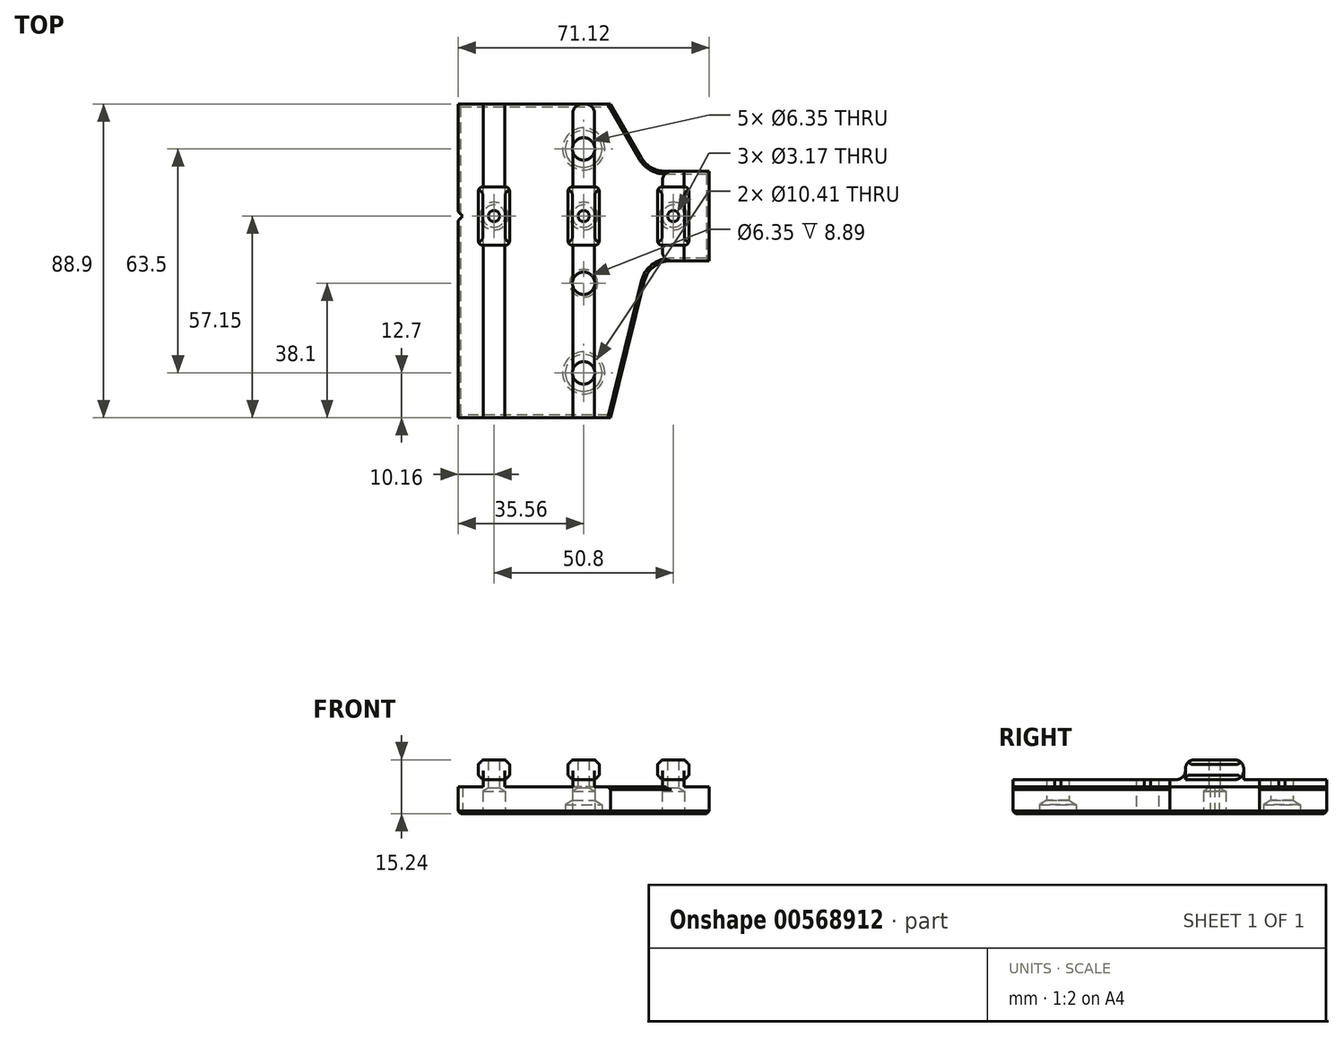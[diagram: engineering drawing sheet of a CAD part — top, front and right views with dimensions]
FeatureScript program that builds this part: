
annotation { "Feature Type Name" : "Feature", "Feature Type Description" : "" }
export const myFeature = defineFeature(function(context is Context, id is Id, definition is map)
    precondition{}
    {
        {
            var Q0;
            Q0=qCreatedBy(makeId("Front.planeOp"),FACE);
            var sketch = newSketch(context, id + "F0", { "sketchPlane" : qUnion([Q0])});
            skLineSegment(sketch, "E0", {"start": v(-35.56, 0) * mm, "end": v(35.56, 0) * mm});
            skLineSegment(sketch, "E1", {"start": v(35.56, 0) * mm, "end": v(35.56, 7.62) * mm});
            skLineSegment(sketch, "E2", {"start": v(35.56, 7.62) * mm, "end": v(28.45, 7.62) * mm});
            skLineSegment(sketch, "E3", {"start": v(28.45, 7.62) * mm, "end": v(28.45, 9.65) * mm});
            skLineSegment(sketch, "E4", {"start": v(28.45, 9.65) * mm, "end": v(22.35, 9.65) * mm});
            skLineSegment(sketch, "E5", {"start": v(22.35, 9.65) * mm, "end": v(22.35, 7.62) * mm});
            skLineSegment(sketch, "E6", {"start": v(22.35, 7.62) * mm, "end": v(3.05, 7.62) * mm});
            skLineSegment(sketch, "E7", {"start": v(3.05, 7.62) * mm, "end": v(3.05, 9.65) * mm});
            skLineSegment(sketch, "E8", {"start": v(3.05, 9.65) * mm, "end": v(-3.05, 9.65) * mm});
            skLineSegment(sketch, "E9", {"start": v(-3.05, 9.65) * mm, "end": v(-3.05, 7.62) * mm});
            skLineSegment(sketch, "E10", {"start": v(-3.05, 7.62) * mm, "end": v(-22.35, 7.62) * mm});
            skLineSegment(sketch, "E11", {"start": v(-22.35, 7.62) * mm, "end": v(-22.35, 9.65) * mm});
            skLineSegment(sketch, "E12", {"start": v(-22.35, 9.65) * mm, "end": v(-28.45, 9.65) * mm});
            skLineSegment(sketch, "E13", {"start": v(-28.45, 9.65) * mm, "end": v(-28.45, 7.62) * mm});
            skLineSegment(sketch, "E14", {"start": v(-28.45, 7.62) * mm, "end": v(-35.56, 7.62) * mm});
            skLineSegment(sketch, "E15", {"start": v(-35.56, 7.62) * mm, "end": v(-35.56, 0) * mm});
            skSolve(sketch);
        }
        {
            var Q0;
            Q0 = qSketchRegion(id + "F0", true);
            extrude(context, id + "F1", {"entities" : qUnion([Q0]), "endBound" : BoundingType.SYMMETRIC, "depth" : 88.9 * mm, "offsetDistance" : 25.4 * mm});
        }
        {
            var Q0;
            Q0=makeQuery(id+"F1.opExtrude","SWEPT_FACE",FACE,{"disambiguationData":[OSD([sQuery(id+"F0.wireOp",EDGE,"E0")])]});
            var sketch = newSketch(context, id + "F2", { "sketchPlane" : qUnion([Q0])});
            skPoint(sketch, "E16", {"position": v(0, -31.75) * mm});
            skPoint(sketch, "E17", {"position": v(25.4, -12.7) * mm});
            skPoint(sketch, "E18", {"position": v(0, -12.7) * mm});
            skPoint(sketch, "E19", {"position": v(-25.4, -12.7) * mm});
            skPoint(sketch, "E20", {"position": v(0, 6.35) * mm});
            skPoint(sketch, "E21", {"position": v(0, 31.75) * mm});
            skSolve(sketch);
        }
        {
            var Q0;
            {var subQ0=sQuery(id+"F0.wireOp",EDGE,"E0");Q0=makeQuery(id+"F2.imprint","IMPRINT",FACE,{"disambiguationData":[TD([[makeQuery(id+"F2.imprint","IMPRINT",EDGE,{"derivedFrom":makeQuery(id+"F1.opExtrude","CAP_EDGE",EDGE,{"disambiguationData":[OSD([subQ0])],"isStart":true})}),1.0]])]});}
            var sketch = newSketch(context, id + "F3", { "sketchPlane" : qUnion([Q0])});
            skLineSegment(sketch, "E22", {"start": v(35.56, -44.45) * mm, "end": v(7.62, -44.45) * mm});
            skLineSegment(sketch, "E23", {"start": v(7.62, -44.45) * mm, "end": v(18.62, -25.4) * mm});
            skLineSegment(sketch, "E24", {"start": v(18.62, -25.4) * mm, "end": v(35.56, -25.4) * mm});
            skLineSegment(sketch, "E25", {"start": v(35.56, -25.4) * mm, "end": v(35.56, -44.45) * mm});
            skLineSegment(sketch, "E26", {"start": v(35.56, 44.45) * mm, "end": v(35.56, 0) * mm});
            skLineSegment(sketch, "E27", {"start": v(35.56, 0) * mm, "end": v(18.62, 0) * mm});
            skLineSegment(sketch, "E28", {"start": v(18.62, 0) * mm, "end": v(7.62, 44.45) * mm});
            skLineSegment(sketch, "E29", {"start": v(7.62, 44.45) * mm, "end": v(35.56, 44.45) * mm});
            skSolve(sketch);
        }
        {
            var Q0;
            Q0=makeQuery(id+"F3.imprint","IMPRINT",FACE,{"disambiguationData":[TD([[makeQuery(id+"F3.imprint","IMPRINT",EDGE,{"derivedFrom":sQuery(id+"F3.wireOp",EDGE,"E22")}),1.0]])]});
            var Q1;
            Q1=makeQuery(id+"F3.imprint","IMPRINT",FACE,{"disambiguationData":[TD([[makeQuery(id+"F3.imprint","IMPRINT",EDGE,{"derivedFrom":sQuery(id+"F3.wireOp",EDGE,"E26")}),-1.0]])]});
            extrude(context, id + "F4", {"entities" : qUnion([Q0, Q1]), "operationType" : NewBodyOperationType.REMOVE, "oppositeDirection" : true, "depth" : 25.4 * mm, "offsetDistance" : 25.4 * mm});
        }
        {
            var Q0;
            Q0=sQuery(id+"F2.wireOp",VERTEX,"E16");
            var Q1;
            Q1=sQuery(id+"F2.wireOp",VERTEX,"E20");
            var Q2;
            Q2=sQuery(id+"F2.wireOp",VERTEX,"E21");
            var Q3;
            Q3=makeQuery(id+"F1.opExtrude","SWEPT_BODY",BODY,{"disambiguationData":[OSD([sQuery(id+"F0.wireOp",EDGE,"E0"),sQuery(id+"F0.wireOp",EDGE,"E1"),sQuery(id+"F0.wireOp",EDGE,"E2"),sQuery(id+"F0.wireOp",EDGE,"E3"),sQuery(id+"F0.wireOp",EDGE,"E4"),sQuery(id+"F0.wireOp",EDGE,"E5"),sQuery(id+"F0.wireOp",EDGE,"E6"),sQuery(id+"F0.wireOp",EDGE,"E7"),sQuery(id+"F0.wireOp",EDGE,"E8"),sQuery(id+"F0.wireOp",EDGE,"E9"),sQuery(id+"F0.wireOp",EDGE,"E10"),sQuery(id+"F0.wireOp",EDGE,"E11"),sQuery(id+"F0.wireOp",EDGE,"E12"),sQuery(id+"F0.wireOp",EDGE,"E13"),sQuery(id+"F0.wireOp",EDGE,"E14"),sQuery(id+"F0.wireOp",EDGE,"E15")])]});
            hole(context, id + "F5", {"style" : HoleStyle.SIMPLE, "endStyle" : HoleEndStyle.THROUGH, "holeDiameter" : 6.35 * mm, "tappedDepth" : 12.7 * mm, "tapClearance" : 3, "startFromSketch" : true, "locations" : qUnion([Q0, Q1, Q2]), "scope" : qUnion([Q3])});
        }
        {
            var Q0;
            Q0=sQuery(id+"F2.wireOp",VERTEX,"E19");
            var Q1;
            Q1=sQuery(id+"F2.wireOp",VERTEX,"E18");
            var Q2;
            Q2=sQuery(id+"F2.wireOp",VERTEX,"E17");
            var Q3;
            Q3=makeQuery(id+"F1.opExtrude","SWEPT_BODY",BODY,{"disambiguationData":[OSD([sQuery(id+"F0.wireOp",EDGE,"E0"),sQuery(id+"F0.wireOp",EDGE,"E1"),sQuery(id+"F0.wireOp",EDGE,"E2"),sQuery(id+"F0.wireOp",EDGE,"E3"),sQuery(id+"F0.wireOp",EDGE,"E4"),sQuery(id+"F0.wireOp",EDGE,"E5"),sQuery(id+"F0.wireOp",EDGE,"E6"),sQuery(id+"F0.wireOp",EDGE,"E7"),sQuery(id+"F0.wireOp",EDGE,"E8"),sQuery(id+"F0.wireOp",EDGE,"E9"),sQuery(id+"F0.wireOp",EDGE,"E10"),sQuery(id+"F0.wireOp",EDGE,"E11"),sQuery(id+"F0.wireOp",EDGE,"E12"),sQuery(id+"F0.wireOp",EDGE,"E13"),sQuery(id+"F0.wireOp",EDGE,"E14"),sQuery(id+"F0.wireOp",EDGE,"E15")])]});
            hole(context, id + "F6", {"style" : HoleStyle.SIMPLE, "endStyle" : HoleEndStyle.BLIND, "holeDiameter" : 6.35 * mm, "holeDepth" : 6.35 * mm, "tappedDepth" : 12.7 * mm, "tapClearance" : 3, "startFromSketch" : true, "locations" : qUnion([Q0, Q1, Q2]), "scope" : qUnion([Q3])});
        }
        {
            var Q0;
            {var subQ0=sQuery(id+"F0.wireOp",EDGE,"E7");var subQ2=sQuery(id+"F0.wireOp",EDGE,"E9");var subQ4=makeQuery(id+"F5.hole-0.opRevolve","SWEPT_FACE",FACE,{"disambiguationData":[OSD([sQuery(id+"F5.hole-0.sketch.wireOp",EDGE,"core_line_2")])]});var subQ5=sQuery(id+"F0.wireOp",EDGE,"E8");Q0=makeQuery(id+"F5.hole-1.boolean.opBoolean","SPLIT",FACE,{"disambiguationData":[TD([makeQuery(id+"F5.hole-0.boolean.opBoolean","COPY",FACE,{"derivedFrom":subQ4})])],"derivedFrom":makeQuery(id+"F5.hole-0.boolean.opBoolean","SPLIT",FACE,{"disambiguationData":[TD([makeQuery(id+"F1.opExtrude","CAP_FACE",FACE,{"disambiguationData":[OSD([sQuery(id+"F0.wireOp",EDGE,"E0"),sQuery(id+"F0.wireOp",EDGE,"E1"),sQuery(id+"F0.wireOp",EDGE,"E2"),sQuery(id+"F0.wireOp",EDGE,"E3"),sQuery(id+"F0.wireOp",EDGE,"E4"),sQuery(id+"F0.wireOp",EDGE,"E5"),sQuery(id+"F0.wireOp",EDGE,"E6"),subQ0,subQ5,subQ2,sQuery(id+"F0.wireOp",EDGE,"E10"),sQuery(id+"F0.wireOp",EDGE,"E11"),sQuery(id+"F0.wireOp",EDGE,"E12"),sQuery(id+"F0.wireOp",EDGE,"E13"),sQuery(id+"F0.wireOp",EDGE,"E14"),sQuery(id+"F0.wireOp",EDGE,"E15")])],"isStart":false})])],"derivedFrom":makeQuery(id+"F1.opExtrude","SWEPT_FACE",FACE,{"disambiguationData":[OSD([subQ5])]})})});}
            var sketch = newSketch(context, id + "F7", { "sketchPlane" : qUnion([Q0])});
            skLineSegment(sketch, "E30.bottom", {"start": v(-29.85, 20.96) * mm, "end": v(-20.96, 20.96) * mm});
            skLineSegment(sketch, "E30.top", {"start": v(-29.85, 4.44) * mm, "end": v(-20.96, 4.44) * mm});
            skLineSegment(sketch, "E30.left", {"start": v(-29.84, 20.96) * mm, "end": v(-29.84, 4.44) * mm});
            skLineSegment(sketch, "E30.right", {"start": v(-20.95, 20.96) * mm, "end": v(-20.95, 4.44) * mm});
            skLineSegment(sketch, "E31.bottom", {"start": v(-4.44, 20.96) * mm, "end": v(4.45, 20.96) * mm});
            skLineSegment(sketch, "E31.top", {"start": v(-4.44, 4.44) * mm, "end": v(4.45, 4.44) * mm});
            skLineSegment(sketch, "E31.left", {"start": v(-4.44, 20.95) * mm, "end": v(-4.45, 4.45) * mm});
            skLineSegment(sketch, "E31.right", {"start": v(4.45, 20.95) * mm, "end": v(4.45, 4.45) * mm});
            skLineSegment(sketch, "E32.bottom", {"start": v(20.96, 20.96) * mm, "end": v(29.85, 20.96) * mm});
            skLineSegment(sketch, "E32.top", {"start": v(20.96, 4.44) * mm, "end": v(29.85, 4.44) * mm});
            skLineSegment(sketch, "E32.left", {"start": v(20.96, 20.96) * mm, "end": v(20.95, 4.44) * mm});
            skLineSegment(sketch, "E32.right", {"start": v(29.84, 20.96) * mm, "end": v(29.84, 4.44) * mm});
            skLineSegment(sketch, "E33", {"start": v(-25.4, 20.96) * mm, "end": v(-25.4, 4.44) * mm, "construction": true});
            skLineSegment(sketch, "E34", {"start": v(0, 20.96) * mm, "end": v(0, 4.44) * mm, "construction": true});
            skLineSegment(sketch, "E35", {"start": v(25.4, 20.96) * mm, "end": v(25.4, 4.44) * mm, "construction": true});
            skSolve(sketch);
        }
        {
            var Q0;
            Q0 = qSketchRegion(id + "F7", true);
            extrude(context, id + "F8", {"entities" : qUnion([Q0]), "operationType" : NewBodyOperationType.ADD, "depth" : 5.6 * mm, "offsetDistance" : 25.4 * mm});
        }
        {
            var Q0;
            Q0=makeQuery(id+"F8.opExtrude","CAP_EDGE",EDGE,{"disambiguationData":[OSD([sQuery(id+"F7.wireOp",EDGE,"E30.left")])],"isStart":true});
            var Q1;
            Q1=makeQuery(id+"F8.opExtrude","CAP_EDGE",EDGE,{"disambiguationData":[OSD([sQuery(id+"F7.wireOp",EDGE,"E30.left")])],"isStart":false});
            var Q2;
            Q2=makeQuery(id+"F8.opExtrude","CAP_EDGE",EDGE,{"disambiguationData":[OSD([sQuery(id+"F7.wireOp",EDGE,"E30.right")])],"isStart":false});
            var Q3;
            Q3=makeQuery(id+"F8.opExtrude","CAP_EDGE",EDGE,{"disambiguationData":[OSD([sQuery(id+"F7.wireOp",EDGE,"E31.left")])],"isStart":true});
            var Q4;
            Q4=makeQuery(id+"F8.opExtrude","CAP_EDGE",EDGE,{"disambiguationData":[OSD([sQuery(id+"F7.wireOp",EDGE,"E31.left")])],"isStart":false});
            var Q5;
            Q5=makeQuery(id+"F8.opExtrude","CAP_EDGE",EDGE,{"disambiguationData":[OSD([sQuery(id+"F7.wireOp",EDGE,"E32.left")])],"isStart":true});
            var Q6;
            Q6=makeQuery(id+"F8.opExtrude","CAP_EDGE",EDGE,{"disambiguationData":[OSD([sQuery(id+"F7.wireOp",EDGE,"E32.left")])],"isStart":false});
            var Q7;
            Q7=makeQuery(id+"F8.opExtrude","CAP_EDGE",EDGE,{"disambiguationData":[OSD([sQuery(id+"F7.wireOp",EDGE,"E31.right")])],"isStart":false});
            var Q8;
            Q8=makeQuery(id+"F8.opExtrude","CAP_EDGE",EDGE,{"disambiguationData":[OSD([sQuery(id+"F7.wireOp",EDGE,"E30.right")])],"isStart":true});
            var Q9;
            Q9=makeQuery(id+"F8.opExtrude","CAP_EDGE",EDGE,{"disambiguationData":[OSD([sQuery(id+"F7.wireOp",EDGE,"E31.right")])],"isStart":true});
            var Q10;
            Q10=makeQuery(id+"F8.opExtrude","CAP_EDGE",EDGE,{"disambiguationData":[OSD([sQuery(id+"F7.wireOp",EDGE,"E32.right")])],"isStart":true});
            var Q11;
            Q11=makeQuery(id+"F8.opExtrude","CAP_EDGE",EDGE,{"disambiguationData":[OSD([sQuery(id+"F7.wireOp",EDGE,"E32.right")])],"isStart":false});
            chamfer(context, id + "F9", {"entities" : qUnion([Q0, Q1, Q2, Q3, Q4, Q5, Q6, Q7, Q8, Q9, Q10, Q11]), "width" : 1.27 * mm, "tangentPropagation" : true});
        }
        {
            var Q0;
            Q0=sQuery(id+"F2.wireOp",VERTEX,"E19");
            var Q1;
            Q1=sQuery(id+"F2.wireOp",VERTEX,"E18");
            var Q2;
            Q2=sQuery(id+"F2.wireOp",VERTEX,"E17");
            var Q3;
            Q3=makeQuery(id+"F1.opExtrude","SWEPT_BODY",BODY,{"disambiguationData":[OSD([sQuery(id+"F0.wireOp",EDGE,"E0"),sQuery(id+"F0.wireOp",EDGE,"E1"),sQuery(id+"F0.wireOp",EDGE,"E2"),sQuery(id+"F0.wireOp",EDGE,"E3"),sQuery(id+"F0.wireOp",EDGE,"E4"),sQuery(id+"F0.wireOp",EDGE,"E5"),sQuery(id+"F0.wireOp",EDGE,"E6"),sQuery(id+"F0.wireOp",EDGE,"E7"),sQuery(id+"F0.wireOp",EDGE,"E8"),sQuery(id+"F0.wireOp",EDGE,"E9"),sQuery(id+"F0.wireOp",EDGE,"E10"),sQuery(id+"F0.wireOp",EDGE,"E11"),sQuery(id+"F0.wireOp",EDGE,"E12"),sQuery(id+"F0.wireOp",EDGE,"E13"),sQuery(id+"F0.wireOp",EDGE,"E14"),sQuery(id+"F0.wireOp",EDGE,"E15")])]});
            hole(context, id + "F10", {"style" : HoleStyle.SIMPLE, "endStyle" : HoleEndStyle.THROUGH, "holeDiameter" : 3.17 * mm, "tappedDepth" : 12.7 * mm, "tapClearance" : 3, "startFromSketch" : true, "locations" : qUnion([Q0, Q1, Q2]), "scope" : qUnion([Q3])});
        }
        {
            var Q0;
            Q0=sQuery(id+"F2.wireOp",VERTEX,"E16");
            var Q1;
            Q1=sQuery(id+"F2.wireOp",VERTEX,"E21");
            var Q2;
            Q2=makeQuery(id+"F1.opExtrude","SWEPT_BODY",BODY,{"disambiguationData":[OSD([sQuery(id+"F0.wireOp",EDGE,"E0"),sQuery(id+"F0.wireOp",EDGE,"E1"),sQuery(id+"F0.wireOp",EDGE,"E2"),sQuery(id+"F0.wireOp",EDGE,"E3"),sQuery(id+"F0.wireOp",EDGE,"E4"),sQuery(id+"F0.wireOp",EDGE,"E5"),sQuery(id+"F0.wireOp",EDGE,"E6"),sQuery(id+"F0.wireOp",EDGE,"E7"),sQuery(id+"F0.wireOp",EDGE,"E8"),sQuery(id+"F0.wireOp",EDGE,"E9"),sQuery(id+"F0.wireOp",EDGE,"E10"),sQuery(id+"F0.wireOp",EDGE,"E11"),sQuery(id+"F0.wireOp",EDGE,"E12"),sQuery(id+"F0.wireOp",EDGE,"E13"),sQuery(id+"F0.wireOp",EDGE,"E14"),sQuery(id+"F0.wireOp",EDGE,"E15")])]});
            hole(context, id + "F11", {"style" : HoleStyle.SIMPLE, "endStyle" : HoleEndStyle.BLIND, "holeDiameter" : 10.4 * mm, "holeDepth" : 2.54 * mm, "tappedDepth" : 12.7 * mm, "tapClearance" : 3, "startFromSketch" : true, "locations" : qUnion([Q0, Q1]), "scope" : qUnion([Q2])});
        }
        {
            var Q0;
            Q0=makeQuery(id+"F6yBhReDyAXkrBv_1.1.F4.boolean.opBoolean","COPY",EDGE,{"derivedFrom":makeQuery(id+"F6yBhReDyAXkrBv_1.1.F4.opExtrude","SWEPT_EDGE",EDGE,{"disambiguationData":[OSD([sQuery(id+"F3.wireOp",EDGE,"E27"),sQuery(id+"F3.wireOp",EDGE,"E28")])]})});
            var Q1;
            Q1=makeQuery(id+"F4.boolean.opBoolean","COPY",EDGE,{"derivedFrom":makeQuery(id+"F4.opExtrude","SWEPT_EDGE",EDGE,{"disambiguationData":[OSD([sQuery(id+"F3.wireOp",EDGE,"E27"),sQuery(id+"F3.wireOp",EDGE,"E28")])]})});
            var Q2;
            Q2=makeQuery(id+"F4.boolean.opBoolean","COPY",EDGE,{"derivedFrom":makeQuery(id+"F4.opExtrude","SWEPT_EDGE",EDGE,{"disambiguationData":[OSD([sQuery(id+"F3.wireOp",EDGE,"E23"),sQuery(id+"F3.wireOp",EDGE,"E24")])]})});
            var Q3;
            Q3=makeQuery(id+"F6yBhReDyAXkrBv_1.1.F4.boolean.opBoolean","COPY",EDGE,{"derivedFrom":makeQuery(id+"F6yBhReDyAXkrBv_1.1.F4.opExtrude","SWEPT_EDGE",EDGE,{"disambiguationData":[OSD([sQuery(id+"F3.wireOp",EDGE,"E23"),sQuery(id+"F3.wireOp",EDGE,"E24")])]})});
            var Q4;
            Q4=makeQuery(id+"F6yBhReDyAXkrBv_1.1.F4.boolean.opBoolean","COPY",EDGE,{"derivedFrom":makeQuery(id+"F6yBhReDyAXkrBv_1.1.F4.opExtrude","SWEPT_EDGE",EDGE,{"disambiguationData":[OSD([sQuery(id+"F0.wireOp",EDGE,"E0"),sQuery(id+"F0.wireOp",EDGE,"E1"),sQuery(id+"F3.wireOp",EDGE,"E24"),sQuery(id+"F3.wireOp",EDGE,"E25")])]})});
            var Q5;
            Q5=makeQuery(id+"F6yBhReDyAXkrBv_1.1.F4.boolean.opBoolean","COPY",EDGE,{"derivedFrom":makeQuery(id+"F6yBhReDyAXkrBv_1.1.F4.opExtrude","SWEPT_EDGE",EDGE,{"disambiguationData":[OSD([sQuery(id+"F0.wireOp",EDGE,"E0"),sQuery(id+"F0.wireOp",EDGE,"E1"),sQuery(id+"F3.wireOp",EDGE,"E26"),sQuery(id+"F3.wireOp",EDGE,"E27")])]})});
            var Q6;
            Q6=makeQuery(id+"F6yBhReDyAXkrBv_1.1.F4.boolean.opBoolean","COPY",EDGE,{"derivedFrom":makeQuery(id+"F6yBhReDyAXkrBv_1.1.F4.opExtrude","SWEPT_EDGE",EDGE,{"disambiguationData":[OSD([sQuery(id+"F0.wireOp",EDGE,"E0"),sQuery(id+"F3.wireOp",EDGE,"E28"),sQuery(id+"F3.wireOp",EDGE,"E29")])]})});
            var Q7;
            Q7=makeQuery(id+"F6yBhReDyAXkrBv_1.1.F4.boolean.opBoolean","COPY",EDGE,{"derivedFrom":makeQuery(id+"F6yBhReDyAXkrBv_1.1.F4.opExtrude","SWEPT_EDGE",EDGE,{"disambiguationData":[OSD([sQuery(id+"F0.wireOp",EDGE,"E0"),sQuery(id+"F3.wireOp",EDGE,"E22"),sQuery(id+"F3.wireOp",EDGE,"E23")])]})});
            var Q8;
            Q8=makeQuery(id+"F4.boolean.opBoolean","COPY",EDGE,{"derivedFrom":makeQuery(id+"F4.opExtrude","SWEPT_EDGE",EDGE,{"disambiguationData":[OSD([sQuery(id+"F0.wireOp",EDGE,"E0"),sQuery(id+"F3.wireOp",EDGE,"E22"),sQuery(id+"F3.wireOp",EDGE,"E23")])]})});
            var Q9;
            Q9=makeQuery(id+"F4.boolean.opBoolean","COPY",EDGE,{"derivedFrom":makeQuery(id+"F4.opExtrude","SWEPT_EDGE",EDGE,{"disambiguationData":[OSD([sQuery(id+"F0.wireOp",EDGE,"E0"),sQuery(id+"F0.wireOp",EDGE,"E1"),sQuery(id+"F3.wireOp",EDGE,"E24"),sQuery(id+"F3.wireOp",EDGE,"E25")])]})});
            var Q10;
            Q10=makeQuery(id+"F4.boolean.opBoolean","COPY",EDGE,{"derivedFrom":makeQuery(id+"F4.opExtrude","SWEPT_EDGE",EDGE,{"disambiguationData":[OSD([sQuery(id+"F0.wireOp",EDGE,"E0"),sQuery(id+"F0.wireOp",EDGE,"E1"),sQuery(id+"F3.wireOp",EDGE,"E26"),sQuery(id+"F3.wireOp",EDGE,"E27")])]})});
            var Q11;
            Q11=makeQuery(id+"F4.boolean.opBoolean","COPY",EDGE,{"derivedFrom":makeQuery(id+"F4.opExtrude","SWEPT_EDGE",EDGE,{"disambiguationData":[OSD([sQuery(id+"F0.wireOp",EDGE,"E0"),sQuery(id+"F3.wireOp",EDGE,"E28"),sQuery(id+"F3.wireOp",EDGE,"E29")])]})});
            fillet(context, id + "F12", {"entities" : qUnion([Q0, Q1, Q2, Q3, Q4, Q5, Q6, Q7, Q8, Q9, Q10, Q11]), "radius" : 7.62 * mm, "tangentPropagation" : true, "allowEdgeOverflow" : false});
        }
        {
            var Q0;
            Q0=makeQuery(id+"F12.opFillet","BLEND_EDGE",EDGE,{"blendedFrom":[makeQuery(id+"F6yBhReDyAXkrBv_1.1.F4.boolean.opBoolean","COPY",EDGE,{"derivedFrom":makeQuery(id+"F6yBhReDyAXkrBv_1.1.F4.opExtrude","SWEPT_EDGE",EDGE,{"disambiguationData":[OSD([sQuery(id+"F0.wireOp",EDGE,"E0"),sQuery(id+"F0.wireOp",EDGE,"E1"),sQuery(id+"F3.wireOp",EDGE,"E26"),sQuery(id+"F3.wireOp",EDGE,"E27")])]})}),makeQuery(id+"F1.opExtrude","SWEPT_FACE",FACE,{"disambiguationData":[OSD([sQuery(id+"F0.wireOp",EDGE,"E13")])]})],"blendedInto":[makeQuery(id+"F1.opExtrude","SWEPT_FACE",FACE,{"disambiguationData":[OSD([sQuery(id+"F0.wireOp",EDGE,"E13")])]})]});
            var Q1;
            Q1=makeQuery(id+"F12.opFillet","BLEND_EDGE",EDGE,{"blendedFrom":[makeQuery(id+"F6yBhReDyAXkrBv_1.1.F4.boolean.opBoolean","COPY",EDGE,{"derivedFrom":makeQuery(id+"F6yBhReDyAXkrBv_1.1.F4.opExtrude","SWEPT_EDGE",EDGE,{"disambiguationData":[OSD([sQuery(id+"F3.wireOp",EDGE,"E27"),sQuery(id+"F3.wireOp",EDGE,"E28")])]})}),makeQuery(id+"F1.opExtrude","SWEPT_FACE",FACE,{"disambiguationData":[OSD([sQuery(id+"F0.wireOp",EDGE,"E11")])]})],"blendedInto":[makeQuery(id+"F1.opExtrude","SWEPT_FACE",FACE,{"disambiguationData":[OSD([sQuery(id+"F0.wireOp",EDGE,"E11")])]})]});
            var Q2;
            {var subQ0=sQuery(id+"F0.wireOp",EDGE,"E10");var subQ1=sQuery(id+"F0.wireOp",EDGE,"E9");var subQ2=sQuery(id+"F0.wireOp",EDGE,"E8");var subQ3=sQuery(id+"F0.wireOp",EDGE,"E0");var subQ4=makeQuery(id+"F1.opExtrude","CAP_FACE",FACE,{"disambiguationData":[OSD([subQ3,sQuery(id+"F0.wireOp",EDGE,"E1"),sQuery(id+"F0.wireOp",EDGE,"E2"),sQuery(id+"F0.wireOp",EDGE,"E3"),sQuery(id+"F0.wireOp",EDGE,"E4"),sQuery(id+"F0.wireOp",EDGE,"E5"),sQuery(id+"F0.wireOp",EDGE,"E6"),sQuery(id+"F0.wireOp",EDGE,"E7"),subQ2,subQ1,subQ0,sQuery(id+"F0.wireOp",EDGE,"E11"),sQuery(id+"F0.wireOp",EDGE,"E12"),sQuery(id+"F0.wireOp",EDGE,"E13"),sQuery(id+"F0.wireOp",EDGE,"E14"),sQuery(id+"F0.wireOp",EDGE,"E15")])],"isStart":false});Q2=makeQuery(id+"F12.opFillet","BLEND_EDGE",EDGE,{"blendedFrom":[makeQuery(id+"F6yBhReDyAXkrBv_1.1.F4.boolean.opBoolean","COPY",EDGE,{"derivedFrom":makeQuery(id+"F6yBhReDyAXkrBv_1.1.F4.opExtrude","SWEPT_EDGE",EDGE,{"disambiguationData":[OSD([subQ3,sQuery(id+"F3.wireOp",EDGE,"E28"),sQuery(id+"F3.wireOp",EDGE,"E29")])]})}),makeQuery(id+"F5.hole-2.boolean.opBoolean","SPLIT",FACE,{"disambiguationData":[TD([subQ4])],"derivedFrom":makeQuery(id+"F5.hole-1.boolean.opBoolean","SPLIT",FACE,{"disambiguationData":[TD([subQ4])],"derivedFrom":makeQuery(id+"F5.hole-0.boolean.opBoolean","SPLIT",FACE,{"disambiguationData":[TD([subQ4])],"derivedFrom":makeQuery(id+"F1.opExtrude","SWEPT_FACE",FACE,{"disambiguationData":[OSD([subQ1])]})})})})],"blendedInto":[makeQuery(id+"F5.hole-2.boolean.opBoolean","SPLIT",FACE,{"disambiguationData":[TD([subQ4])],"derivedFrom":makeQuery(id+"F5.hole-1.boolean.opBoolean","SPLIT",FACE,{"disambiguationData":[TD([subQ4])],"derivedFrom":makeQuery(id+"F5.hole-0.boolean.opBoolean","SPLIT",FACE,{"disambiguationData":[TD([subQ4])],"derivedFrom":makeQuery(id+"F1.opExtrude","SWEPT_FACE",FACE,{"disambiguationData":[OSD([subQ1])]})})})})]});}
            var Q3;
            {var subQ0=sQuery(id+"F0.wireOp",EDGE,"E8");var subQ1=sQuery(id+"F0.wireOp",EDGE,"E7");var subQ2=sQuery(id+"F0.wireOp",EDGE,"E6");var subQ3=sQuery(id+"F0.wireOp",EDGE,"E0");var subQ4=makeQuery(id+"F1.opExtrude","CAP_FACE",FACE,{"disambiguationData":[OSD([subQ3,sQuery(id+"F0.wireOp",EDGE,"E1"),sQuery(id+"F0.wireOp",EDGE,"E2"),sQuery(id+"F0.wireOp",EDGE,"E3"),sQuery(id+"F0.wireOp",EDGE,"E4"),sQuery(id+"F0.wireOp",EDGE,"E5"),subQ2,subQ1,subQ0,sQuery(id+"F0.wireOp",EDGE,"E9"),sQuery(id+"F0.wireOp",EDGE,"E10"),sQuery(id+"F0.wireOp",EDGE,"E11"),sQuery(id+"F0.wireOp",EDGE,"E12"),sQuery(id+"F0.wireOp",EDGE,"E13"),sQuery(id+"F0.wireOp",EDGE,"E14"),sQuery(id+"F0.wireOp",EDGE,"E15")])],"isStart":false});Q3=makeQuery(id+"F12.opFillet","BLEND_EDGE",EDGE,{"blendedFrom":[makeQuery(id+"F4.boolean.opBoolean","COPY",EDGE,{"derivedFrom":makeQuery(id+"F4.opExtrude","SWEPT_EDGE",EDGE,{"disambiguationData":[OSD([subQ3,sQuery(id+"F3.wireOp",EDGE,"E28"),sQuery(id+"F3.wireOp",EDGE,"E29")])]})}),makeQuery(id+"F5.hole-2.boolean.opBoolean","SPLIT",FACE,{"disambiguationData":[TD([subQ4])],"derivedFrom":makeQuery(id+"F5.hole-1.boolean.opBoolean","SPLIT",FACE,{"disambiguationData":[TD([subQ4])],"derivedFrom":makeQuery(id+"F5.hole-0.boolean.opBoolean","SPLIT",FACE,{"disambiguationData":[TD([subQ4])],"derivedFrom":makeQuery(id+"F1.opExtrude","SWEPT_FACE",FACE,{"disambiguationData":[OSD([subQ1])]})})})})],"blendedInto":[makeQuery(id+"F5.hole-2.boolean.opBoolean","SPLIT",FACE,{"disambiguationData":[TD([subQ4])],"derivedFrom":makeQuery(id+"F5.hole-1.boolean.opBoolean","SPLIT",FACE,{"disambiguationData":[TD([subQ4])],"derivedFrom":makeQuery(id+"F5.hole-0.boolean.opBoolean","SPLIT",FACE,{"disambiguationData":[TD([subQ4])],"derivedFrom":makeQuery(id+"F1.opExtrude","SWEPT_FACE",FACE,{"disambiguationData":[OSD([subQ1])]})})})})]});}
            var Q4;
            Q4=makeQuery(id+"F12.opFillet","BLEND_EDGE",EDGE,{"blendedFrom":[makeQuery(id+"F4.boolean.opBoolean","COPY",EDGE,{"derivedFrom":makeQuery(id+"F4.opExtrude","SWEPT_EDGE",EDGE,{"disambiguationData":[OSD([sQuery(id+"F3.wireOp",EDGE,"E27"),sQuery(id+"F3.wireOp",EDGE,"E28")])]})}),makeQuery(id+"F1.opExtrude","SWEPT_FACE",FACE,{"disambiguationData":[OSD([sQuery(id+"F0.wireOp",EDGE,"E5")])]})],"blendedInto":[makeQuery(id+"F1.opExtrude","SWEPT_FACE",FACE,{"disambiguationData":[OSD([sQuery(id+"F0.wireOp",EDGE,"E5")])]})]});
            var Q5;
            Q5=makeQuery(id+"F12.opFillet","BLEND_EDGE",EDGE,{"blendedFrom":[makeQuery(id+"F4.boolean.opBoolean","COPY",EDGE,{"derivedFrom":makeQuery(id+"F4.opExtrude","SWEPT_EDGE",EDGE,{"disambiguationData":[OSD([sQuery(id+"F0.wireOp",EDGE,"E0"),sQuery(id+"F0.wireOp",EDGE,"E1"),sQuery(id+"F3.wireOp",EDGE,"E26"),sQuery(id+"F3.wireOp",EDGE,"E27")])]})}),makeQuery(id+"F1.opExtrude","SWEPT_FACE",FACE,{"disambiguationData":[OSD([sQuery(id+"F0.wireOp",EDGE,"E3")])]})],"blendedInto":[makeQuery(id+"F1.opExtrude","SWEPT_FACE",FACE,{"disambiguationData":[OSD([sQuery(id+"F0.wireOp",EDGE,"E3")])]})]});
            var Q6;
            Q6=makeQuery(id+"F12.opFillet","BLEND_EDGE",EDGE,{"blendedFrom":[makeQuery(id+"F4.boolean.opBoolean","COPY",EDGE,{"derivedFrom":makeQuery(id+"F4.opExtrude","SWEPT_EDGE",EDGE,{"disambiguationData":[OSD([sQuery(id+"F0.wireOp",EDGE,"E0"),sQuery(id+"F0.wireOp",EDGE,"E1"),sQuery(id+"F3.wireOp",EDGE,"E24"),sQuery(id+"F3.wireOp",EDGE,"E25")])]})}),makeQuery(id+"F1.opExtrude","SWEPT_FACE",FACE,{"disambiguationData":[OSD([sQuery(id+"F0.wireOp",EDGE,"E3")])]})],"blendedInto":[makeQuery(id+"F1.opExtrude","SWEPT_FACE",FACE,{"disambiguationData":[OSD([sQuery(id+"F0.wireOp",EDGE,"E3")])]})]});
            var Q7;
            Q7=makeQuery(id+"F12.opFillet","BLEND_EDGE",EDGE,{"blendedFrom":[makeQuery(id+"F4.boolean.opBoolean","COPY",EDGE,{"derivedFrom":makeQuery(id+"F4.opExtrude","SWEPT_EDGE",EDGE,{"disambiguationData":[OSD([sQuery(id+"F3.wireOp",EDGE,"E23"),sQuery(id+"F3.wireOp",EDGE,"E24")])]})}),makeQuery(id+"F1.opExtrude","SWEPT_FACE",FACE,{"disambiguationData":[OSD([sQuery(id+"F0.wireOp",EDGE,"E5")])]})],"blendedInto":[makeQuery(id+"F1.opExtrude","SWEPT_FACE",FACE,{"disambiguationData":[OSD([sQuery(id+"F0.wireOp",EDGE,"E5")])]})]});
            var Q8;
            Q8=makeQuery(id+"F12.opFillet","BLEND_EDGE",EDGE,{"blendedFrom":[makeQuery(id+"F6yBhReDyAXkrBv_1.1.F4.boolean.opBoolean","COPY",EDGE,{"derivedFrom":makeQuery(id+"F6yBhReDyAXkrBv_1.1.F4.opExtrude","SWEPT_EDGE",EDGE,{"disambiguationData":[OSD([sQuery(id+"F0.wireOp",EDGE,"E0"),sQuery(id+"F0.wireOp",EDGE,"E1"),sQuery(id+"F3.wireOp",EDGE,"E24"),sQuery(id+"F3.wireOp",EDGE,"E25")])]})}),makeQuery(id+"F1.opExtrude","SWEPT_FACE",FACE,{"disambiguationData":[OSD([sQuery(id+"F0.wireOp",EDGE,"E13")])]})],"blendedInto":[makeQuery(id+"F1.opExtrude","SWEPT_FACE",FACE,{"disambiguationData":[OSD([sQuery(id+"F0.wireOp",EDGE,"E13")])]})]});
            var Q9;
            Q9=makeQuery(id+"F12.opFillet","BLEND_EDGE",EDGE,{"blendedFrom":[makeQuery(id+"F6yBhReDyAXkrBv_1.1.F4.boolean.opBoolean","COPY",EDGE,{"derivedFrom":makeQuery(id+"F6yBhReDyAXkrBv_1.1.F4.opExtrude","SWEPT_EDGE",EDGE,{"disambiguationData":[OSD([sQuery(id+"F3.wireOp",EDGE,"E23"),sQuery(id+"F3.wireOp",EDGE,"E24")])]})}),makeQuery(id+"F1.opExtrude","SWEPT_FACE",FACE,{"disambiguationData":[OSD([sQuery(id+"F0.wireOp",EDGE,"E11")])]})],"blendedInto":[makeQuery(id+"F1.opExtrude","SWEPT_FACE",FACE,{"disambiguationData":[OSD([sQuery(id+"F0.wireOp",EDGE,"E11")])]})]});
            var Q10;
            Q10=makeQuery(id+"F1.opExtrude","CAP_EDGE",EDGE,{"disambiguationData":[OSD([sQuery(id+"F0.wireOp",EDGE,"E9")])],"isStart":true});
            var Q11;
            Q11=makeQuery(id+"F1.opExtrude","CAP_EDGE",EDGE,{"disambiguationData":[OSD([sQuery(id+"F0.wireOp",EDGE,"E7")])],"isStart":true});
            var Q12;
            {var subQ0=sQuery(id+"F0.wireOp",EDGE,"E10");var subQ1=sQuery(id+"F0.wireOp",EDGE,"E9");var subQ2=sQuery(id+"F0.wireOp",EDGE,"E8");var subQ3=makeQuery(id+"F1.opExtrude","CAP_FACE",FACE,{"disambiguationData":[OSD([sQuery(id+"F0.wireOp",EDGE,"E0"),sQuery(id+"F0.wireOp",EDGE,"E1"),sQuery(id+"F0.wireOp",EDGE,"E2"),sQuery(id+"F0.wireOp",EDGE,"E3"),sQuery(id+"F0.wireOp",EDGE,"E4"),sQuery(id+"F0.wireOp",EDGE,"E5"),sQuery(id+"F0.wireOp",EDGE,"E6"),sQuery(id+"F0.wireOp",EDGE,"E7"),subQ2,subQ1,subQ0,sQuery(id+"F0.wireOp",EDGE,"E11"),sQuery(id+"F0.wireOp",EDGE,"E12"),sQuery(id+"F0.wireOp",EDGE,"E13"),sQuery(id+"F0.wireOp",EDGE,"E14"),sQuery(id+"F0.wireOp",EDGE,"E15")])],"isStart":false});Q12=makeQuery(id+"F5.hole-2.boolean.opBoolean","INTERSECT",EDGE,{"disambiguationData":[OD(1.0)],"derivedFrom":[makeQuery(id+"F5.hole-1.boolean.opBoolean","SPLIT",FACE,{"disambiguationData":[TD([subQ3])],"derivedFrom":makeQuery(id+"F5.hole-0.boolean.opBoolean","SPLIT",FACE,{"disambiguationData":[TD([subQ3])],"derivedFrom":makeQuery(id+"F1.opExtrude","SWEPT_FACE",FACE,{"disambiguationData":[OSD([subQ1])]})})}),makeQuery(id+"F5.hole-2.opRevolve","SWEPT_FACE",FACE,{"disambiguationData":[OSD([sQuery(id+"F5.hole-2.sketch.wireOp",EDGE,"core_line_2")])]})]});}
            var Q13;
            {var subQ0=sQuery(id+"F0.wireOp",EDGE,"E10");var subQ1=sQuery(id+"F0.wireOp",EDGE,"E9");var subQ2=sQuery(id+"F0.wireOp",EDGE,"E8");var subQ3=makeQuery(id+"F1.opExtrude","CAP_FACE",FACE,{"disambiguationData":[OSD([sQuery(id+"F0.wireOp",EDGE,"E0"),sQuery(id+"F0.wireOp",EDGE,"E1"),sQuery(id+"F0.wireOp",EDGE,"E2"),sQuery(id+"F0.wireOp",EDGE,"E3"),sQuery(id+"F0.wireOp",EDGE,"E4"),sQuery(id+"F0.wireOp",EDGE,"E5"),sQuery(id+"F0.wireOp",EDGE,"E6"),sQuery(id+"F0.wireOp",EDGE,"E7"),subQ2,subQ1,subQ0,sQuery(id+"F0.wireOp",EDGE,"E11"),sQuery(id+"F0.wireOp",EDGE,"E12"),sQuery(id+"F0.wireOp",EDGE,"E13"),sQuery(id+"F0.wireOp",EDGE,"E14"),sQuery(id+"F0.wireOp",EDGE,"E15")])],"isStart":false});Q13=makeQuery(id+"F5.hole-2.boolean.opBoolean","INTERSECT",EDGE,{"disambiguationData":[OD(0.0)],"derivedFrom":[makeQuery(id+"F5.hole-1.boolean.opBoolean","SPLIT",FACE,{"disambiguationData":[TD([subQ3])],"derivedFrom":makeQuery(id+"F5.hole-0.boolean.opBoolean","SPLIT",FACE,{"disambiguationData":[TD([subQ3])],"derivedFrom":makeQuery(id+"F1.opExtrude","SWEPT_FACE",FACE,{"disambiguationData":[OSD([subQ1])]})})}),makeQuery(id+"F5.hole-2.opRevolve","SWEPT_FACE",FACE,{"disambiguationData":[OSD([sQuery(id+"F5.hole-2.sketch.wireOp",EDGE,"core_line_2")])]})]});}
            var Q14;
            {var subQ0=sQuery(id+"F0.wireOp",EDGE,"E8");var subQ1=sQuery(id+"F0.wireOp",EDGE,"E7");var subQ2=sQuery(id+"F0.wireOp",EDGE,"E6");var subQ3=makeQuery(id+"F1.opExtrude","CAP_FACE",FACE,{"disambiguationData":[OSD([sQuery(id+"F0.wireOp",EDGE,"E0"),sQuery(id+"F0.wireOp",EDGE,"E1"),sQuery(id+"F0.wireOp",EDGE,"E2"),sQuery(id+"F0.wireOp",EDGE,"E3"),sQuery(id+"F0.wireOp",EDGE,"E4"),sQuery(id+"F0.wireOp",EDGE,"E5"),subQ2,subQ1,subQ0,sQuery(id+"F0.wireOp",EDGE,"E9"),sQuery(id+"F0.wireOp",EDGE,"E10"),sQuery(id+"F0.wireOp",EDGE,"E11"),sQuery(id+"F0.wireOp",EDGE,"E12"),sQuery(id+"F0.wireOp",EDGE,"E13"),sQuery(id+"F0.wireOp",EDGE,"E14"),sQuery(id+"F0.wireOp",EDGE,"E15")])],"isStart":false});Q14=makeQuery(id+"F5.hole-2.boolean.opBoolean","INTERSECT",EDGE,{"disambiguationData":[OD(0.0)],"derivedFrom":[makeQuery(id+"F5.hole-1.boolean.opBoolean","SPLIT",FACE,{"disambiguationData":[TD([subQ3])],"derivedFrom":makeQuery(id+"F5.hole-0.boolean.opBoolean","SPLIT",FACE,{"disambiguationData":[TD([subQ3])],"derivedFrom":makeQuery(id+"F1.opExtrude","SWEPT_FACE",FACE,{"disambiguationData":[OSD([subQ1])]})})}),makeQuery(id+"F5.hole-2.opRevolve","SWEPT_FACE",FACE,{"disambiguationData":[OSD([sQuery(id+"F5.hole-2.sketch.wireOp",EDGE,"core_line_2")])]})]});}
            var Q15;
            {var subQ0=sQuery(id+"F0.wireOp",EDGE,"E8");var subQ1=sQuery(id+"F0.wireOp",EDGE,"E7");var subQ2=sQuery(id+"F0.wireOp",EDGE,"E6");var subQ3=makeQuery(id+"F1.opExtrude","CAP_FACE",FACE,{"disambiguationData":[OSD([sQuery(id+"F0.wireOp",EDGE,"E0"),sQuery(id+"F0.wireOp",EDGE,"E1"),sQuery(id+"F0.wireOp",EDGE,"E2"),sQuery(id+"F0.wireOp",EDGE,"E3"),sQuery(id+"F0.wireOp",EDGE,"E4"),sQuery(id+"F0.wireOp",EDGE,"E5"),subQ2,subQ1,subQ0,sQuery(id+"F0.wireOp",EDGE,"E9"),sQuery(id+"F0.wireOp",EDGE,"E10"),sQuery(id+"F0.wireOp",EDGE,"E11"),sQuery(id+"F0.wireOp",EDGE,"E12"),sQuery(id+"F0.wireOp",EDGE,"E13"),sQuery(id+"F0.wireOp",EDGE,"E14"),sQuery(id+"F0.wireOp",EDGE,"E15")])],"isStart":false});Q15=makeQuery(id+"F5.hole-2.boolean.opBoolean","INTERSECT",EDGE,{"disambiguationData":[OD(1.0)],"derivedFrom":[makeQuery(id+"F5.hole-1.boolean.opBoolean","SPLIT",FACE,{"disambiguationData":[TD([subQ3])],"derivedFrom":makeQuery(id+"F5.hole-0.boolean.opBoolean","SPLIT",FACE,{"disambiguationData":[TD([subQ3])],"derivedFrom":makeQuery(id+"F1.opExtrude","SWEPT_FACE",FACE,{"disambiguationData":[OSD([subQ1])]})})}),makeQuery(id+"F5.hole-2.opRevolve","SWEPT_FACE",FACE,{"disambiguationData":[OSD([sQuery(id+"F5.hole-2.sketch.wireOp",EDGE,"core_line_2")])]})]});}
            var Q16;
            {var subQ0=sQuery(id+"F0.wireOp",EDGE,"E8");var subQ1=sQuery(id+"F0.wireOp",EDGE,"E7");var subQ2=sQuery(id+"F0.wireOp",EDGE,"E6");Q16=makeQuery(id+"F5.hole-1.boolean.opBoolean","INTERSECT",EDGE,{"disambiguationData":[OD(0.0)],"derivedFrom":[makeQuery(id+"F5.hole-0.boolean.opBoolean","SPLIT",FACE,{"disambiguationData":[TD([makeQuery(id+"F1.opExtrude","CAP_FACE",FACE,{"disambiguationData":[OSD([sQuery(id+"F0.wireOp",EDGE,"E0"),sQuery(id+"F0.wireOp",EDGE,"E1"),sQuery(id+"F0.wireOp",EDGE,"E2"),sQuery(id+"F0.wireOp",EDGE,"E3"),sQuery(id+"F0.wireOp",EDGE,"E4"),sQuery(id+"F0.wireOp",EDGE,"E5"),subQ2,subQ1,subQ0,sQuery(id+"F0.wireOp",EDGE,"E9"),sQuery(id+"F0.wireOp",EDGE,"E10"),sQuery(id+"F0.wireOp",EDGE,"E11"),sQuery(id+"F0.wireOp",EDGE,"E12"),sQuery(id+"F0.wireOp",EDGE,"E13"),sQuery(id+"F0.wireOp",EDGE,"E14"),sQuery(id+"F0.wireOp",EDGE,"E15")])],"isStart":false})])],"derivedFrom":makeQuery(id+"F1.opExtrude","SWEPT_FACE",FACE,{"disambiguationData":[OSD([subQ1])]})}),makeQuery(id+"F5.hole-1.opRevolve","SWEPT_FACE",FACE,{"disambiguationData":[OSD([sQuery(id+"F5.hole-1.sketch.wireOp",EDGE,"core_line_2")])]})]});}
            var Q17;
            {var subQ0=sQuery(id+"F0.wireOp",EDGE,"E8");var subQ1=sQuery(id+"F0.wireOp",EDGE,"E7");var subQ2=sQuery(id+"F0.wireOp",EDGE,"E6");Q17=makeQuery(id+"F5.hole-1.boolean.opBoolean","INTERSECT",EDGE,{"disambiguationData":[OD(1.0)],"derivedFrom":[makeQuery(id+"F5.hole-0.boolean.opBoolean","SPLIT",FACE,{"disambiguationData":[TD([makeQuery(id+"F1.opExtrude","CAP_FACE",FACE,{"disambiguationData":[OSD([sQuery(id+"F0.wireOp",EDGE,"E0"),sQuery(id+"F0.wireOp",EDGE,"E1"),sQuery(id+"F0.wireOp",EDGE,"E2"),sQuery(id+"F0.wireOp",EDGE,"E3"),sQuery(id+"F0.wireOp",EDGE,"E4"),sQuery(id+"F0.wireOp",EDGE,"E5"),subQ2,subQ1,subQ0,sQuery(id+"F0.wireOp",EDGE,"E9"),sQuery(id+"F0.wireOp",EDGE,"E10"),sQuery(id+"F0.wireOp",EDGE,"E11"),sQuery(id+"F0.wireOp",EDGE,"E12"),sQuery(id+"F0.wireOp",EDGE,"E13"),sQuery(id+"F0.wireOp",EDGE,"E14"),sQuery(id+"F0.wireOp",EDGE,"E15")])],"isStart":false})])],"derivedFrom":makeQuery(id+"F1.opExtrude","SWEPT_FACE",FACE,{"disambiguationData":[OSD([subQ1])]})}),makeQuery(id+"F5.hole-1.opRevolve","SWEPT_FACE",FACE,{"disambiguationData":[OSD([sQuery(id+"F5.hole-1.sketch.wireOp",EDGE,"core_line_2")])]})]});}
            var Q18;
            {var subQ0=sQuery(id+"F0.wireOp",EDGE,"E10");var subQ1=sQuery(id+"F0.wireOp",EDGE,"E9");var subQ2=sQuery(id+"F0.wireOp",EDGE,"E8");Q18=makeQuery(id+"F5.hole-1.boolean.opBoolean","INTERSECT",EDGE,{"disambiguationData":[OD(1.0)],"derivedFrom":[makeQuery(id+"F5.hole-0.boolean.opBoolean","SPLIT",FACE,{"disambiguationData":[TD([makeQuery(id+"F1.opExtrude","CAP_FACE",FACE,{"disambiguationData":[OSD([sQuery(id+"F0.wireOp",EDGE,"E0"),sQuery(id+"F0.wireOp",EDGE,"E1"),sQuery(id+"F0.wireOp",EDGE,"E2"),sQuery(id+"F0.wireOp",EDGE,"E3"),sQuery(id+"F0.wireOp",EDGE,"E4"),sQuery(id+"F0.wireOp",EDGE,"E5"),sQuery(id+"F0.wireOp",EDGE,"E6"),sQuery(id+"F0.wireOp",EDGE,"E7"),subQ2,subQ1,subQ0,sQuery(id+"F0.wireOp",EDGE,"E11"),sQuery(id+"F0.wireOp",EDGE,"E12"),sQuery(id+"F0.wireOp",EDGE,"E13"),sQuery(id+"F0.wireOp",EDGE,"E14"),sQuery(id+"F0.wireOp",EDGE,"E15")])],"isStart":false})])],"derivedFrom":makeQuery(id+"F1.opExtrude","SWEPT_FACE",FACE,{"disambiguationData":[OSD([subQ1])]})}),makeQuery(id+"F5.hole-1.opRevolve","SWEPT_FACE",FACE,{"disambiguationData":[OSD([sQuery(id+"F5.hole-1.sketch.wireOp",EDGE,"core_line_2")])]})]});}
            var Q19;
            {var subQ0=sQuery(id+"F0.wireOp",EDGE,"E10");var subQ1=sQuery(id+"F0.wireOp",EDGE,"E9");var subQ2=sQuery(id+"F0.wireOp",EDGE,"E8");Q19=makeQuery(id+"F5.hole-1.boolean.opBoolean","INTERSECT",EDGE,{"disambiguationData":[OD(0.0)],"derivedFrom":[makeQuery(id+"F5.hole-0.boolean.opBoolean","SPLIT",FACE,{"disambiguationData":[TD([makeQuery(id+"F1.opExtrude","CAP_FACE",FACE,{"disambiguationData":[OSD([sQuery(id+"F0.wireOp",EDGE,"E0"),sQuery(id+"F0.wireOp",EDGE,"E1"),sQuery(id+"F0.wireOp",EDGE,"E2"),sQuery(id+"F0.wireOp",EDGE,"E3"),sQuery(id+"F0.wireOp",EDGE,"E4"),sQuery(id+"F0.wireOp",EDGE,"E5"),sQuery(id+"F0.wireOp",EDGE,"E6"),sQuery(id+"F0.wireOp",EDGE,"E7"),subQ2,subQ1,subQ0,sQuery(id+"F0.wireOp",EDGE,"E11"),sQuery(id+"F0.wireOp",EDGE,"E12"),sQuery(id+"F0.wireOp",EDGE,"E13"),sQuery(id+"F0.wireOp",EDGE,"E14"),sQuery(id+"F0.wireOp",EDGE,"E15")])],"isStart":false})])],"derivedFrom":makeQuery(id+"F1.opExtrude","SWEPT_FACE",FACE,{"disambiguationData":[OSD([subQ1])]})}),makeQuery(id+"F5.hole-1.opRevolve","SWEPT_FACE",FACE,{"disambiguationData":[OSD([sQuery(id+"F5.hole-1.sketch.wireOp",EDGE,"core_line_2")])]})]});}
            var Q20;
            Q20=makeQuery(id+"F5.hole-0.boolean.opBoolean","INTERSECT",EDGE,{"disambiguationData":[OD(0.0)],"derivedFrom":[makeQuery(id+"F1.opExtrude","SWEPT_FACE",FACE,{"disambiguationData":[OSD([sQuery(id+"F0.wireOp",EDGE,"E9")])]}),makeQuery(id+"F5.hole-0.opRevolve","SWEPT_FACE",FACE,{"disambiguationData":[OSD([sQuery(id+"F5.hole-0.sketch.wireOp",EDGE,"core_line_2")])]})]});
            var Q21;
            Q21=makeQuery(id+"F5.hole-0.boolean.opBoolean","INTERSECT",EDGE,{"disambiguationData":[OD(1.0)],"derivedFrom":[makeQuery(id+"F1.opExtrude","SWEPT_FACE",FACE,{"disambiguationData":[OSD([sQuery(id+"F0.wireOp",EDGE,"E9")])]}),makeQuery(id+"F5.hole-0.opRevolve","SWEPT_FACE",FACE,{"disambiguationData":[OSD([sQuery(id+"F5.hole-0.sketch.wireOp",EDGE,"core_line_2")])]})]});
            var Q22;
            Q22=makeQuery(id+"F5.hole-0.boolean.opBoolean","INTERSECT",EDGE,{"disambiguationData":[OD(0.0)],"derivedFrom":[makeQuery(id+"F1.opExtrude","SWEPT_FACE",FACE,{"disambiguationData":[OSD([sQuery(id+"F0.wireOp",EDGE,"E7")])]}),makeQuery(id+"F5.hole-0.opRevolve","SWEPT_FACE",FACE,{"disambiguationData":[OSD([sQuery(id+"F5.hole-0.sketch.wireOp",EDGE,"core_line_2")])]})]});
            var Q23;
            Q23=makeQuery(id+"F5.hole-0.boolean.opBoolean","INTERSECT",EDGE,{"disambiguationData":[OD(1.0)],"derivedFrom":[makeQuery(id+"F1.opExtrude","SWEPT_FACE",FACE,{"disambiguationData":[OSD([sQuery(id+"F0.wireOp",EDGE,"E7")])]}),makeQuery(id+"F5.hole-0.opRevolve","SWEPT_FACE",FACE,{"disambiguationData":[OSD([sQuery(id+"F5.hole-0.sketch.wireOp",EDGE,"core_line_2")])]})]});
            fillet(context, id + "F13", {"entities" : qUnion([Q0, Q1, Q2, Q3, Q4, Q5, Q6, Q7, Q8, Q9, Q10, Q11, Q12, Q13, Q14, Q15, Q16, Q17, Q18, Q19, Q20, Q21, Q22, Q23]), "radius" : 2.54 * mm, "tangentPropagation" : true, "allowEdgeOverflow" : false});
        }
        {
            var Q0;
            Q0=makeQuery(id+"F8.opExtrude","CAP_EDGE",EDGE,{"disambiguationData":[OSD([sQuery(id+"F7.wireOp",EDGE,"E30.top")])],"isStart":false});
            var Q1;
            {var subQ0=sQuery(id+"F7.wireOp",EDGE,"E30.top");Q1=makeQuery(id+"F8.boolean.opBoolean","SPLIT",EDGE,{"disambiguationData":[topologyDisambiguationEdgeConnected([makeQuery(id+"F1.opExtrude","SWEPT_FACE",FACE,{"disambiguationData":[OSD([sQuery(id+"F0.wireOp",EDGE,"E12")])]}),makeQuery(id+"F8.opExtrude","SWEPT_FACE",FACE,{"disambiguationData":[OSD([subQ0])]})])],"derivedFrom":makeQuery(id+"F8.opExtrude","CAP_EDGE",EDGE,{"disambiguationData":[OSD([subQ0])],"isStart":true})});}
            var Q2;
            {var subQ0=sQuery(id+"F7.wireOp",EDGE,"E31.top");Q2=makeQuery(id+"F8.boolean.opBoolean","SPLIT",EDGE,{"disambiguationData":[topologyDisambiguationEdgeConnected([makeQuery(id+"F1.opExtrude","SWEPT_FACE",FACE,{"disambiguationData":[OSD([sQuery(id+"F0.wireOp",EDGE,"E8")])]}),makeQuery(id+"F8.opExtrude","SWEPT_FACE",FACE,{"disambiguationData":[OSD([subQ0])]})])],"derivedFrom":makeQuery(id+"F8.opExtrude","CAP_EDGE",EDGE,{"disambiguationData":[OSD([subQ0])],"isStart":true})});}
            var Q3;
            Q3=makeQuery(id+"F8.opExtrude","CAP_EDGE",EDGE,{"disambiguationData":[OSD([sQuery(id+"F7.wireOp",EDGE,"E31.top")])],"isStart":false});
            var Q4;
            Q4=makeQuery(id+"F8.opExtrude","CAP_EDGE",EDGE,{"disambiguationData":[OSD([sQuery(id+"F7.wireOp",EDGE,"E30.bottom")])],"isStart":false});
            var Q5;
            Q5=makeQuery(id+"F8.opExtrude","CAP_EDGE",EDGE,{"disambiguationData":[OSD([sQuery(id+"F7.wireOp",EDGE,"E31.bottom")])],"isStart":false});
            var Q6;
            Q6=makeQuery(id+"F8.opExtrude","CAP_EDGE",EDGE,{"disambiguationData":[OSD([sQuery(id+"F7.wireOp",EDGE,"E32.top")])],"isStart":false});
            var Q7;
            {var subQ0=sQuery(id+"F7.wireOp",EDGE,"E32.top");Q7=makeQuery(id+"F8.boolean.opBoolean","SPLIT",EDGE,{"disambiguationData":[topologyDisambiguationEdgeConnected([makeQuery(id+"F1.opExtrude","SWEPT_FACE",FACE,{"disambiguationData":[OSD([sQuery(id+"F0.wireOp",EDGE,"E4")])]}),makeQuery(id+"F8.opExtrude","SWEPT_FACE",FACE,{"disambiguationData":[OSD([subQ0])]})])],"derivedFrom":makeQuery(id+"F8.opExtrude","CAP_EDGE",EDGE,{"disambiguationData":[OSD([subQ0])],"isStart":true})});}
            var Q8;
            Q8=makeQuery(id+"F8.opExtrude","CAP_EDGE",EDGE,{"disambiguationData":[OSD([sQuery(id+"F7.wireOp",EDGE,"E32.bottom")])],"isStart":false});
            var Q9;
            {var subQ0=sQuery(id+"F7.wireOp",EDGE,"E32.bottom");Q9=makeQuery(id+"F8.boolean.opBoolean","SPLIT",EDGE,{"disambiguationData":[topologyDisambiguationEdgeConnected([makeQuery(id+"F1.opExtrude","SWEPT_FACE",FACE,{"disambiguationData":[OSD([sQuery(id+"F0.wireOp",EDGE,"E4")])]}),makeQuery(id+"F8.opExtrude","SWEPT_FACE",FACE,{"disambiguationData":[OSD([subQ0])]})])],"derivedFrom":makeQuery(id+"F8.opExtrude","CAP_EDGE",EDGE,{"disambiguationData":[OSD([subQ0])],"isStart":true})});}
            var Q10;
            {var subQ0=sQuery(id+"F7.wireOp",EDGE,"E31.bottom");Q10=makeQuery(id+"F8.boolean.opBoolean","SPLIT",EDGE,{"disambiguationData":[topologyDisambiguationEdgeConnected([makeQuery(id+"F1.opExtrude","SWEPT_FACE",FACE,{"disambiguationData":[OSD([sQuery(id+"F0.wireOp",EDGE,"E8")])]}),makeQuery(id+"F8.opExtrude","SWEPT_FACE",FACE,{"disambiguationData":[OSD([subQ0])]})])],"derivedFrom":makeQuery(id+"F8.opExtrude","CAP_EDGE",EDGE,{"disambiguationData":[OSD([subQ0])],"isStart":true})});}
            var Q11;
            {var subQ0=sQuery(id+"F7.wireOp",EDGE,"E30.bottom");Q11=makeQuery(id+"F8.boolean.opBoolean","SPLIT",EDGE,{"disambiguationData":[topologyDisambiguationEdgeConnected([makeQuery(id+"F1.opExtrude","SWEPT_FACE",FACE,{"disambiguationData":[OSD([sQuery(id+"F0.wireOp",EDGE,"E12")])]}),makeQuery(id+"F8.opExtrude","SWEPT_FACE",FACE,{"disambiguationData":[OSD([subQ0])]})])],"derivedFrom":makeQuery(id+"F8.opExtrude","CAP_EDGE",EDGE,{"disambiguationData":[OSD([subQ0])],"isStart":true})});}
            fillet(context, id + "F14", {"entities" : qUnion([Q0, Q1, Q2, Q3, Q4, Q5, Q6, Q7, Q8, Q9, Q10, Q11]), "radius" : 2.54 * mm, "tangentPropagation" : true, "allowEdgeOverflow" : false});
        }
        {
            var Q0;
            {var subQ0=sQuery(id+"F0.wireOp",EDGE,"E9");var subQ1=sQuery(id+"F0.wireOp",EDGE,"E8");var subQ2=sQuery(id+"F0.wireOp",EDGE,"E7");var subQ3=sQuery(id+"F0.wireOp",EDGE,"E6");var subQ4=sQuery(id+"F0.wireOp",EDGE,"E0");var subQ5=makeQuery(id+"F1.opExtrude","CAP_FACE",FACE,{"disambiguationData":[OSD([subQ4,sQuery(id+"F0.wireOp",EDGE,"E1"),sQuery(id+"F0.wireOp",EDGE,"E2"),sQuery(id+"F0.wireOp",EDGE,"E3"),sQuery(id+"F0.wireOp",EDGE,"E4"),sQuery(id+"F0.wireOp",EDGE,"E5"),subQ3,subQ2,subQ1,subQ0,sQuery(id+"F0.wireOp",EDGE,"E10"),sQuery(id+"F0.wireOp",EDGE,"E11"),sQuery(id+"F0.wireOp",EDGE,"E12"),sQuery(id+"F0.wireOp",EDGE,"E13"),sQuery(id+"F0.wireOp",EDGE,"E14"),sQuery(id+"F0.wireOp",EDGE,"E15")])],"isStart":false});var subQ7=makeQuery(id+"F1.opExtrude","SWEPT_FACE",FACE,{"disambiguationData":[OSD([subQ2])]});var subQ11=makeQuery(id+"F1.opExtrude","SWEPT_FACE",FACE,{"disambiguationData":[OSD([subQ1])]});Q0=makeQuery(id+"F13.opFillet","BLEND_EDGE",EDGE,{"blendedFrom":[makeQuery(id+"F12.opFillet","BLEND_EDGE",EDGE,{"blendedFrom":[makeQuery(id+"F4.boolean.opBoolean","COPY",EDGE,{"derivedFrom":makeQuery(id+"F4.opExtrude","SWEPT_EDGE",EDGE,{"disambiguationData":[OSD([subQ4,sQuery(id+"F3.wireOp",EDGE,"E28"),sQuery(id+"F3.wireOp",EDGE,"E29")])]})}),makeQuery(id+"F5.hole-2.boolean.opBoolean","SPLIT",FACE,{"disambiguationData":[TD([subQ5])],"derivedFrom":makeQuery(id+"F5.hole-1.boolean.opBoolean","SPLIT",FACE,{"disambiguationData":[TD([subQ5])],"derivedFrom":makeQuery(id+"F5.hole-0.boolean.opBoolean","SPLIT",FACE,{"disambiguationData":[TD([subQ5])],"derivedFrom":subQ7})})})],"blendedInto":[makeQuery(id+"F5.hole-2.boolean.opBoolean","SPLIT",FACE,{"disambiguationData":[TD([subQ5])],"derivedFrom":makeQuery(id+"F5.hole-1.boolean.opBoolean","SPLIT",FACE,{"disambiguationData":[TD([subQ5])],"derivedFrom":makeQuery(id+"F5.hole-0.boolean.opBoolean","SPLIT",FACE,{"disambiguationData":[TD([subQ5])],"derivedFrom":subQ7})})})]}),makeQuery(id+"F5.hole-2.boolean.opBoolean","SPLIT",FACE,{"disambiguationData":[TD([subQ5])],"derivedFrom":makeQuery(id+"F5.hole-1.boolean.opBoolean","SPLIT",FACE,{"disambiguationData":[TD([subQ5])],"derivedFrom":makeQuery(id+"F5.hole-0.boolean.opBoolean","SPLIT",FACE,{"disambiguationData":[TD([subQ5])],"derivedFrom":subQ11})})})],"blendedInto":[makeQuery(id+"F5.hole-2.boolean.opBoolean","SPLIT",FACE,{"disambiguationData":[TD([subQ5])],"derivedFrom":makeQuery(id+"F5.hole-1.boolean.opBoolean","SPLIT",FACE,{"disambiguationData":[TD([subQ5])],"derivedFrom":makeQuery(id+"F5.hole-0.boolean.opBoolean","SPLIT",FACE,{"disambiguationData":[TD([subQ5])],"derivedFrom":subQ11})})})]});}
            var Q1;
            {var subQ0=sQuery(id+"F0.wireOp",EDGE,"E7");var subQ1=makeQuery(id+"F1.opExtrude","SWEPT_FACE",FACE,{"disambiguationData":[OSD([subQ0])]});var subQ2=sQuery(id+"F0.wireOp",EDGE,"E9");var subQ4=makeQuery(id+"F5.hole-1.opRevolve","SWEPT_FACE",FACE,{"disambiguationData":[OSD([sQuery(id+"F5.hole-1.sketch.wireOp",EDGE,"core_line_2")])]});var subQ5=makeQuery(id+"F5.hole-2.opRevolve","SWEPT_FACE",FACE,{"disambiguationData":[OSD([sQuery(id+"F5.hole-2.sketch.wireOp",EDGE,"core_line_2")])]});var subQ6=sQuery(id+"F0.wireOp",EDGE,"E8");var subQ7=sQuery(id+"F0.wireOp",EDGE,"E6");var subQ8=makeQuery(id+"F1.opExtrude","CAP_FACE",FACE,{"disambiguationData":[OSD([sQuery(id+"F0.wireOp",EDGE,"E0"),sQuery(id+"F0.wireOp",EDGE,"E1"),sQuery(id+"F0.wireOp",EDGE,"E2"),sQuery(id+"F0.wireOp",EDGE,"E3"),sQuery(id+"F0.wireOp",EDGE,"E4"),sQuery(id+"F0.wireOp",EDGE,"E5"),subQ7,subQ0,subQ6,subQ2,sQuery(id+"F0.wireOp",EDGE,"E10"),sQuery(id+"F0.wireOp",EDGE,"E11"),sQuery(id+"F0.wireOp",EDGE,"E12"),sQuery(id+"F0.wireOp",EDGE,"E13"),sQuery(id+"F0.wireOp",EDGE,"E14"),sQuery(id+"F0.wireOp",EDGE,"E15")])],"isStart":false});var subQ10=makeQuery(id+"F1.opExtrude","SWEPT_FACE",FACE,{"disambiguationData":[OSD([subQ6])]});Q1=makeQuery(id+"F13.opFillet","BLEND_EDGE",EDGE,{"blendedFrom":[makeQuery(id+"F5.hole-2.boolean.opBoolean","INTERSECT",EDGE,{"disambiguationData":[OD(1.0)],"derivedFrom":[makeQuery(id+"F5.hole-1.boolean.opBoolean","SPLIT",FACE,{"disambiguationData":[TD([subQ8])],"derivedFrom":makeQuery(id+"F5.hole-0.boolean.opBoolean","SPLIT",FACE,{"disambiguationData":[TD([subQ8])],"derivedFrom":subQ1})}),subQ5]}),makeQuery(id+"F5.hole-2.boolean.opBoolean","SPLIT",FACE,{"disambiguationData":[TD([makeQuery(id+"F5.hole-1.boolean.opBoolean","COPY",FACE,{"derivedFrom":subQ4})])],"derivedFrom":makeQuery(id+"F5.hole-1.boolean.opBoolean","SPLIT",FACE,{"disambiguationData":[TD([subQ8])],"derivedFrom":makeQuery(id+"F5.hole-0.boolean.opBoolean","SPLIT",FACE,{"disambiguationData":[TD([subQ8])],"derivedFrom":subQ10})})})],"blendedInto":[makeQuery(id+"F5.hole-2.boolean.opBoolean","SPLIT",FACE,{"disambiguationData":[TD([makeQuery(id+"F5.hole-1.boolean.opBoolean","COPY",FACE,{"derivedFrom":subQ4})])],"derivedFrom":makeQuery(id+"F5.hole-1.boolean.opBoolean","SPLIT",FACE,{"disambiguationData":[TD([subQ8])],"derivedFrom":makeQuery(id+"F5.hole-0.boolean.opBoolean","SPLIT",FACE,{"disambiguationData":[TD([subQ8])],"derivedFrom":subQ10})})})]});}
            var Q2;
            {var subQ1=makeQuery(id+"F5.hole-1.opRevolve","SWEPT_FACE",FACE,{"disambiguationData":[OSD([sQuery(id+"F5.hole-1.sketch.wireOp",EDGE,"core_line_2")])]});var subQ2=sQuery(id+"F0.wireOp",EDGE,"E9");var subQ4=sQuery(id+"F0.wireOp",EDGE,"E7");var subQ5=makeQuery(id+"F1.opExtrude","SWEPT_FACE",FACE,{"disambiguationData":[OSD([subQ4])]});var subQ6=makeQuery(id+"F5.hole-0.opRevolve","SWEPT_FACE",FACE,{"disambiguationData":[OSD([sQuery(id+"F5.hole-0.sketch.wireOp",EDGE,"core_line_2")])]});var subQ7=sQuery(id+"F0.wireOp",EDGE,"E8");var subQ8=sQuery(id+"F0.wireOp",EDGE,"E6");var subQ9=makeQuery(id+"F1.opExtrude","CAP_FACE",FACE,{"disambiguationData":[OSD([sQuery(id+"F0.wireOp",EDGE,"E0"),sQuery(id+"F0.wireOp",EDGE,"E1"),sQuery(id+"F0.wireOp",EDGE,"E2"),sQuery(id+"F0.wireOp",EDGE,"E3"),sQuery(id+"F0.wireOp",EDGE,"E4"),sQuery(id+"F0.wireOp",EDGE,"E5"),subQ8,subQ4,subQ7,subQ2,sQuery(id+"F0.wireOp",EDGE,"E10"),sQuery(id+"F0.wireOp",EDGE,"E11"),sQuery(id+"F0.wireOp",EDGE,"E12"),sQuery(id+"F0.wireOp",EDGE,"E13"),sQuery(id+"F0.wireOp",EDGE,"E14"),sQuery(id+"F0.wireOp",EDGE,"E15")])],"isStart":false});var subQ10=makeQuery(id+"F1.opExtrude","SWEPT_FACE",FACE,{"disambiguationData":[OSD([subQ7])]});Q2=makeQuery(id+"F13.opFillet","BLEND_EDGE",EDGE,{"blendedFrom":[makeQuery(id+"F5.hole-1.boolean.opBoolean","INTERSECT",EDGE,{"disambiguationData":[OD(1.0)],"derivedFrom":[makeQuery(id+"F5.hole-0.boolean.opBoolean","SPLIT",FACE,{"disambiguationData":[TD([subQ9])],"derivedFrom":subQ5}),subQ1]}),makeQuery(id+"F8.boolean.opBoolean","SPLIT",FACE,{"disambiguationData":[TD([makeQuery(id+"F5.hole-1.boolean.opBoolean","COPY",FACE,{"derivedFrom":subQ1})])],"derivedFrom":makeQuery(id+"F5.hole-1.boolean.opBoolean","SPLIT",FACE,{"disambiguationData":[TD([makeQuery(id+"F5.hole-0.boolean.opBoolean","COPY",FACE,{"derivedFrom":subQ6})])],"derivedFrom":makeQuery(id+"F5.hole-0.boolean.opBoolean","SPLIT",FACE,{"disambiguationData":[TD([subQ9])],"derivedFrom":subQ10})})})],"blendedInto":[makeQuery(id+"F8.boolean.opBoolean","SPLIT",FACE,{"disambiguationData":[TD([makeQuery(id+"F5.hole-1.boolean.opBoolean","COPY",FACE,{"derivedFrom":subQ1})])],"derivedFrom":makeQuery(id+"F5.hole-1.boolean.opBoolean","SPLIT",FACE,{"disambiguationData":[TD([makeQuery(id+"F5.hole-0.boolean.opBoolean","COPY",FACE,{"derivedFrom":subQ6})])],"derivedFrom":makeQuery(id+"F5.hole-0.boolean.opBoolean","SPLIT",FACE,{"disambiguationData":[TD([subQ9])],"derivedFrom":subQ10})})})]});}
            var Q3;
            {var subQ1=sQuery(id+"F3.wireOp",EDGE,"E27");var subQ2=makeQuery(id+"F1.opExtrude","SWEPT_FACE",FACE,{"disambiguationData":[OSD([sQuery(id+"F0.wireOp",EDGE,"E11")])]});Q3=makeQuery(id+"F13.opFillet","BLEND_EDGE",EDGE,{"blendedFrom":[makeQuery(id+"F12.opFillet","BLEND_EDGE",EDGE,{"blendedFrom":[makeQuery(id+"F6yBhReDyAXkrBv_1.1.F4.boolean.opBoolean","COPY",EDGE,{"derivedFrom":makeQuery(id+"F6yBhReDyAXkrBv_1.1.F4.opExtrude","SWEPT_EDGE",EDGE,{"disambiguationData":[OSD([subQ1,sQuery(id+"F3.wireOp",EDGE,"E28")])]})}),subQ2],"blendedInto":[subQ2]}),makeQuery(id+"F8.boolean.opBoolean","SPLIT",FACE,{"disambiguationData":[TD([makeQuery(id+"F6yBhReDyAXkrBv_1.1.F4.boolean.opBoolean","COPY",FACE,{"derivedFrom":makeQuery(id+"F6yBhReDyAXkrBv_1.1.F4.opExtrude","SWEPT_FACE",FACE,{"disambiguationData":[OSD([subQ1])]})})])],"derivedFrom":makeQuery(id+"F1.opExtrude","SWEPT_FACE",FACE,{"disambiguationData":[OSD([sQuery(id+"F0.wireOp",EDGE,"E12")])]})})],"blendedInto":[makeQuery(id+"F8.boolean.opBoolean","SPLIT",FACE,{"disambiguationData":[TD([makeQuery(id+"F6yBhReDyAXkrBv_1.1.F4.boolean.opBoolean","COPY",FACE,{"derivedFrom":makeQuery(id+"F6yBhReDyAXkrBv_1.1.F4.opExtrude","SWEPT_FACE",FACE,{"disambiguationData":[OSD([subQ1])]})})])],"derivedFrom":makeQuery(id+"F1.opExtrude","SWEPT_FACE",FACE,{"disambiguationData":[OSD([sQuery(id+"F0.wireOp",EDGE,"E12")])]})})]});}
            var Q4;
            {var subQ1=sQuery(id+"F3.wireOp",EDGE,"E27");var subQ2=makeQuery(id+"F1.opExtrude","SWEPT_FACE",FACE,{"disambiguationData":[OSD([sQuery(id+"F0.wireOp",EDGE,"E3")])]});Q4=makeQuery(id+"F13.opFillet","BLEND_EDGE",EDGE,{"blendedFrom":[makeQuery(id+"F12.opFillet","BLEND_EDGE",EDGE,{"blendedFrom":[makeQuery(id+"F4.boolean.opBoolean","COPY",EDGE,{"derivedFrom":makeQuery(id+"F4.opExtrude","SWEPT_EDGE",EDGE,{"disambiguationData":[OSD([sQuery(id+"F0.wireOp",EDGE,"E0"),sQuery(id+"F0.wireOp",EDGE,"E1"),sQuery(id+"F3.wireOp",EDGE,"E26"),subQ1])]})}),subQ2],"blendedInto":[subQ2]}),makeQuery(id+"F8.boolean.opBoolean","SPLIT",FACE,{"disambiguationData":[TD([makeQuery(id+"F4.boolean.opBoolean","COPY",FACE,{"derivedFrom":makeQuery(id+"F4.opExtrude","SWEPT_FACE",FACE,{"disambiguationData":[OSD([subQ1])]})})])],"derivedFrom":makeQuery(id+"F1.opExtrude","SWEPT_FACE",FACE,{"disambiguationData":[OSD([sQuery(id+"F0.wireOp",EDGE,"E4")])]})})],"blendedInto":[makeQuery(id+"F8.boolean.opBoolean","SPLIT",FACE,{"disambiguationData":[TD([makeQuery(id+"F4.boolean.opBoolean","COPY",FACE,{"derivedFrom":makeQuery(id+"F4.opExtrude","SWEPT_FACE",FACE,{"disambiguationData":[OSD([subQ1])]})})])],"derivedFrom":makeQuery(id+"F1.opExtrude","SWEPT_FACE",FACE,{"disambiguationData":[OSD([sQuery(id+"F0.wireOp",EDGE,"E4")])]})})]});}
            var Q5;
            {var subQ1=makeQuery(id+"F5.hole-0.opRevolve","SWEPT_FACE",FACE,{"disambiguationData":[OSD([sQuery(id+"F5.hole-0.sketch.wireOp",EDGE,"core_line_2")])]});var subQ2=makeQuery(id+"F5.hole-0.boolean.opBoolean","COPY",FACE,{"derivedFrom":subQ1});var subQ3=sQuery(id+"F0.wireOp",EDGE,"E9");var subQ4=makeQuery(id+"F1.opExtrude","SWEPT_FACE",FACE,{"disambiguationData":[OSD([subQ3])]});var subQ5=sQuery(id+"F0.wireOp",EDGE,"E7");var subQ7=sQuery(id+"F0.wireOp",EDGE,"E8");Q5=makeQuery(id+"F13.opFillet","BLEND_EDGE",EDGE,{"blendedFrom":[makeQuery(id+"F5.hole-0.boolean.opBoolean","INTERSECT",EDGE,{"disambiguationData":[OD(1.0)],"derivedFrom":[subQ4,subQ1]}),makeQuery(id+"F8.boolean.opBoolean","SPLIT",FACE,{"disambiguationData":[TD([subQ2])],"derivedFrom":makeQuery(id+"F5.hole-1.boolean.opBoolean","SPLIT",FACE,{"disambiguationData":[TD([subQ2])],"derivedFrom":makeQuery(id+"F5.hole-0.boolean.opBoolean","SPLIT",FACE,{"disambiguationData":[TD([makeQuery(id+"F1.opExtrude","CAP_FACE",FACE,{"disambiguationData":[OSD([sQuery(id+"F0.wireOp",EDGE,"E0"),sQuery(id+"F0.wireOp",EDGE,"E1"),sQuery(id+"F0.wireOp",EDGE,"E2"),sQuery(id+"F0.wireOp",EDGE,"E3"),sQuery(id+"F0.wireOp",EDGE,"E4"),sQuery(id+"F0.wireOp",EDGE,"E5"),sQuery(id+"F0.wireOp",EDGE,"E6"),subQ5,subQ7,subQ3,sQuery(id+"F0.wireOp",EDGE,"E10"),sQuery(id+"F0.wireOp",EDGE,"E11"),sQuery(id+"F0.wireOp",EDGE,"E12"),sQuery(id+"F0.wireOp",EDGE,"E13"),sQuery(id+"F0.wireOp",EDGE,"E14"),sQuery(id+"F0.wireOp",EDGE,"E15")])],"isStart":false})])],"derivedFrom":makeQuery(id+"F1.opExtrude","SWEPT_FACE",FACE,{"disambiguationData":[OSD([subQ7])]})})})})],"blendedInto":[makeQuery(id+"F8.boolean.opBoolean","SPLIT",FACE,{"disambiguationData":[TD([subQ2])],"derivedFrom":makeQuery(id+"F5.hole-1.boolean.opBoolean","SPLIT",FACE,{"disambiguationData":[TD([subQ2])],"derivedFrom":makeQuery(id+"F5.hole-0.boolean.opBoolean","SPLIT",FACE,{"disambiguationData":[TD([makeQuery(id+"F1.opExtrude","CAP_FACE",FACE,{"disambiguationData":[OSD([sQuery(id+"F0.wireOp",EDGE,"E0"),sQuery(id+"F0.wireOp",EDGE,"E1"),sQuery(id+"F0.wireOp",EDGE,"E2"),sQuery(id+"F0.wireOp",EDGE,"E3"),sQuery(id+"F0.wireOp",EDGE,"E4"),sQuery(id+"F0.wireOp",EDGE,"E5"),sQuery(id+"F0.wireOp",EDGE,"E6"),subQ5,subQ7,subQ3,sQuery(id+"F0.wireOp",EDGE,"E10"),sQuery(id+"F0.wireOp",EDGE,"E11"),sQuery(id+"F0.wireOp",EDGE,"E12"),sQuery(id+"F0.wireOp",EDGE,"E13"),sQuery(id+"F0.wireOp",EDGE,"E14"),sQuery(id+"F0.wireOp",EDGE,"E15")])],"isStart":false})])],"derivedFrom":makeQuery(id+"F1.opExtrude","SWEPT_FACE",FACE,{"disambiguationData":[OSD([subQ7])]})})})})]});}
            var Q6;
            {var subQ1=sQuery(id+"F3.wireOp",EDGE,"E24");var subQ2=makeQuery(id+"F1.opExtrude","SWEPT_FACE",FACE,{"disambiguationData":[OSD([sQuery(id+"F0.wireOp",EDGE,"E11")])]});Q6=makeQuery(id+"F13.opFillet","BLEND_EDGE",EDGE,{"blendedFrom":[makeQuery(id+"F12.opFillet","BLEND_EDGE",EDGE,{"blendedFrom":[makeQuery(id+"F6yBhReDyAXkrBv_1.1.F4.boolean.opBoolean","COPY",EDGE,{"derivedFrom":makeQuery(id+"F6yBhReDyAXkrBv_1.1.F4.opExtrude","SWEPT_EDGE",EDGE,{"disambiguationData":[OSD([sQuery(id+"F3.wireOp",EDGE,"E23"),subQ1])]})}),subQ2],"blendedInto":[subQ2]}),makeQuery(id+"F8.boolean.opBoolean","SPLIT",FACE,{"disambiguationData":[TD([makeQuery(id+"F6yBhReDyAXkrBv_1.1.F4.boolean.opBoolean","COPY",FACE,{"derivedFrom":makeQuery(id+"F6yBhReDyAXkrBv_1.1.F4.opExtrude","SWEPT_FACE",FACE,{"disambiguationData":[OSD([subQ1])]})})])],"derivedFrom":makeQuery(id+"F1.opExtrude","SWEPT_FACE",FACE,{"disambiguationData":[OSD([sQuery(id+"F0.wireOp",EDGE,"E12")])]})})],"blendedInto":[makeQuery(id+"F8.boolean.opBoolean","SPLIT",FACE,{"disambiguationData":[TD([makeQuery(id+"F6yBhReDyAXkrBv_1.1.F4.boolean.opBoolean","COPY",FACE,{"derivedFrom":makeQuery(id+"F6yBhReDyAXkrBv_1.1.F4.opExtrude","SWEPT_FACE",FACE,{"disambiguationData":[OSD([subQ1])]})})])],"derivedFrom":makeQuery(id+"F1.opExtrude","SWEPT_FACE",FACE,{"disambiguationData":[OSD([sQuery(id+"F0.wireOp",EDGE,"E12")])]})})]});}
            var Q7;
            {var subQ0=sQuery(id+"F0.wireOp",EDGE,"E9");var subQ1=sQuery(id+"F0.wireOp",EDGE,"E8");var subQ2=sQuery(id+"F0.wireOp",EDGE,"E7");var subQ3=makeQuery(id+"F1.opExtrude","SWEPT_FACE",FACE,{"disambiguationData":[OSD([subQ2])]});var subQ4=makeQuery(id+"F5.hole-0.opRevolve","SWEPT_FACE",FACE,{"disambiguationData":[OSD([sQuery(id+"F5.hole-0.sketch.wireOp",EDGE,"core_line_2")])]});Q7=makeQuery(id+"F13.opFillet","BLEND_EDGE",EDGE,{"blendedFrom":[makeQuery(id+"F5.hole-0.boolean.opBoolean","INTERSECT",EDGE,{"disambiguationData":[OD(0.0)],"derivedFrom":[subQ3,subQ4]}),makeQuery(id+"F5.hole-0.boolean.opBoolean","SPLIT",FACE,{"disambiguationData":[TD([makeQuery(id+"F1.opExtrude","CAP_FACE",FACE,{"disambiguationData":[OSD([sQuery(id+"F0.wireOp",EDGE,"E0"),sQuery(id+"F0.wireOp",EDGE,"E1"),sQuery(id+"F0.wireOp",EDGE,"E2"),sQuery(id+"F0.wireOp",EDGE,"E3"),sQuery(id+"F0.wireOp",EDGE,"E4"),sQuery(id+"F0.wireOp",EDGE,"E5"),sQuery(id+"F0.wireOp",EDGE,"E6"),subQ2,subQ1,subQ0,sQuery(id+"F0.wireOp",EDGE,"E10"),sQuery(id+"F0.wireOp",EDGE,"E11"),sQuery(id+"F0.wireOp",EDGE,"E12"),sQuery(id+"F0.wireOp",EDGE,"E13"),sQuery(id+"F0.wireOp",EDGE,"E14"),sQuery(id+"F0.wireOp",EDGE,"E15")])],"isStart":true})])],"derivedFrom":makeQuery(id+"F1.opExtrude","SWEPT_FACE",FACE,{"disambiguationData":[OSD([subQ1])]})})],"blendedInto":[makeQuery(id+"F5.hole-0.boolean.opBoolean","SPLIT",FACE,{"disambiguationData":[TD([makeQuery(id+"F1.opExtrude","CAP_FACE",FACE,{"disambiguationData":[OSD([sQuery(id+"F0.wireOp",EDGE,"E0"),sQuery(id+"F0.wireOp",EDGE,"E1"),sQuery(id+"F0.wireOp",EDGE,"E2"),sQuery(id+"F0.wireOp",EDGE,"E3"),sQuery(id+"F0.wireOp",EDGE,"E4"),sQuery(id+"F0.wireOp",EDGE,"E5"),sQuery(id+"F0.wireOp",EDGE,"E6"),subQ2,subQ1,subQ0,sQuery(id+"F0.wireOp",EDGE,"E10"),sQuery(id+"F0.wireOp",EDGE,"E11"),sQuery(id+"F0.wireOp",EDGE,"E12"),sQuery(id+"F0.wireOp",EDGE,"E13"),sQuery(id+"F0.wireOp",EDGE,"E14"),sQuery(id+"F0.wireOp",EDGE,"E15")])],"isStart":true})])],"derivedFrom":makeQuery(id+"F1.opExtrude","SWEPT_FACE",FACE,{"disambiguationData":[OSD([subQ1])]})})]});}
            var Q8;
            {var subQ1=sQuery(id+"F3.wireOp",EDGE,"E24");var subQ2=makeQuery(id+"F1.opExtrude","SWEPT_FACE",FACE,{"disambiguationData":[OSD([sQuery(id+"F0.wireOp",EDGE,"E3")])]});Q8=makeQuery(id+"F13.opFillet","BLEND_EDGE",EDGE,{"blendedFrom":[makeQuery(id+"F12.opFillet","BLEND_EDGE",EDGE,{"blendedFrom":[makeQuery(id+"F4.boolean.opBoolean","COPY",EDGE,{"derivedFrom":makeQuery(id+"F4.opExtrude","SWEPT_EDGE",EDGE,{"disambiguationData":[OSD([sQuery(id+"F0.wireOp",EDGE,"E0"),sQuery(id+"F0.wireOp",EDGE,"E1"),subQ1,sQuery(id+"F3.wireOp",EDGE,"E25")])]})}),subQ2],"blendedInto":[subQ2]}),makeQuery(id+"F8.boolean.opBoolean","SPLIT",FACE,{"disambiguationData":[TD([makeQuery(id+"F4.boolean.opBoolean","COPY",FACE,{"derivedFrom":makeQuery(id+"F4.opExtrude","SWEPT_FACE",FACE,{"disambiguationData":[OSD([subQ1])]})})])],"derivedFrom":makeQuery(id+"F1.opExtrude","SWEPT_FACE",FACE,{"disambiguationData":[OSD([sQuery(id+"F0.wireOp",EDGE,"E4")])]})})],"blendedInto":[makeQuery(id+"F8.boolean.opBoolean","SPLIT",FACE,{"disambiguationData":[TD([makeQuery(id+"F4.boolean.opBoolean","COPY",FACE,{"derivedFrom":makeQuery(id+"F4.opExtrude","SWEPT_FACE",FACE,{"disambiguationData":[OSD([subQ1])]})})])],"derivedFrom":makeQuery(id+"F1.opExtrude","SWEPT_FACE",FACE,{"disambiguationData":[OSD([sQuery(id+"F0.wireOp",EDGE,"E4")])]})})]});}
            var Q9;
            Q9=makeQuery(id+"F1.opExtrude","SWEPT_FACE",FACE,{"disambiguationData":[OSD([sQuery(id+"F0.wireOp",EDGE,"E0")])]});
            var Q10;
            Q10=makeQuery(id+"F12.opFillet","BLEND_EDGE",EDGE,{"blendedFrom":[makeQuery(id+"F6yBhReDyAXkrBv_1.1.F4.boolean.opBoolean","COPY",EDGE,{"derivedFrom":makeQuery(id+"F6yBhReDyAXkrBv_1.1.F4.opExtrude","SWEPT_EDGE",EDGE,{"disambiguationData":[OSD([sQuery(id+"F0.wireOp",EDGE,"E0"),sQuery(id+"F0.wireOp",EDGE,"E1"),sQuery(id+"F3.wireOp",EDGE,"E26"),sQuery(id+"F3.wireOp",EDGE,"E27")])]})}),makeQuery(id+"F1.opExtrude","SWEPT_FACE",FACE,{"disambiguationData":[OSD([sQuery(id+"F0.wireOp",EDGE,"E14")])]})],"blendedInto":[makeQuery(id+"F1.opExtrude","SWEPT_FACE",FACE,{"disambiguationData":[OSD([sQuery(id+"F0.wireOp",EDGE,"E14")])]})]});
            var Q11;
            Q11=makeQuery(id+"F12.opFillet","BLEND_EDGE",EDGE,{"blendedFrom":[makeQuery(id+"F6yBhReDyAXkrBv_1.1.F4.boolean.opBoolean","COPY",EDGE,{"derivedFrom":makeQuery(id+"F6yBhReDyAXkrBv_1.1.F4.opExtrude","SWEPT_EDGE",EDGE,{"disambiguationData":[OSD([sQuery(id+"F3.wireOp",EDGE,"E27"),sQuery(id+"F3.wireOp",EDGE,"E28")])]})}),makeQuery(id+"F1.opExtrude","SWEPT_FACE",FACE,{"disambiguationData":[OSD([sQuery(id+"F0.wireOp",EDGE,"E10")])]})],"blendedInto":[makeQuery(id+"F1.opExtrude","SWEPT_FACE",FACE,{"disambiguationData":[OSD([sQuery(id+"F0.wireOp",EDGE,"E10")])]})]});
            var Q12;
            Q12=makeQuery(id+"F12.opFillet","BLEND_EDGE",EDGE,{"blendedFrom":[makeQuery(id+"F4.boolean.opBoolean","COPY",EDGE,{"derivedFrom":makeQuery(id+"F4.opExtrude","SWEPT_EDGE",EDGE,{"disambiguationData":[OSD([sQuery(id+"F3.wireOp",EDGE,"E27"),sQuery(id+"F3.wireOp",EDGE,"E28")])]})}),makeQuery(id+"F1.opExtrude","SWEPT_FACE",FACE,{"disambiguationData":[OSD([sQuery(id+"F0.wireOp",EDGE,"E6")])]})],"blendedInto":[makeQuery(id+"F1.opExtrude","SWEPT_FACE",FACE,{"disambiguationData":[OSD([sQuery(id+"F0.wireOp",EDGE,"E6")])]})]});
            var Q13;
            Q13=makeQuery(id+"F12.opFillet","BLEND_EDGE",EDGE,{"blendedFrom":[makeQuery(id+"F4.boolean.opBoolean","COPY",EDGE,{"derivedFrom":makeQuery(id+"F4.opExtrude","SWEPT_EDGE",EDGE,{"disambiguationData":[OSD([sQuery(id+"F0.wireOp",EDGE,"E0"),sQuery(id+"F0.wireOp",EDGE,"E1"),sQuery(id+"F3.wireOp",EDGE,"E26"),sQuery(id+"F3.wireOp",EDGE,"E27")])]})}),makeQuery(id+"F1.opExtrude","SWEPT_FACE",FACE,{"disambiguationData":[OSD([sQuery(id+"F0.wireOp",EDGE,"E2")])]})],"blendedInto":[makeQuery(id+"F1.opExtrude","SWEPT_FACE",FACE,{"disambiguationData":[OSD([sQuery(id+"F0.wireOp",EDGE,"E2")])]})]});
            var Q14;
            Q14=makeQuery(id+"F12.opFillet","BLEND_EDGE",EDGE,{"blendedFrom":[makeQuery(id+"F4.boolean.opBoolean","COPY",EDGE,{"derivedFrom":makeQuery(id+"F4.opExtrude","SWEPT_EDGE",EDGE,{"disambiguationData":[OSD([sQuery(id+"F3.wireOp",EDGE,"E23"),sQuery(id+"F3.wireOp",EDGE,"E24")])]})}),makeQuery(id+"F1.opExtrude","SWEPT_FACE",FACE,{"disambiguationData":[OSD([sQuery(id+"F0.wireOp",EDGE,"E6")])]})],"blendedInto":[makeQuery(id+"F1.opExtrude","SWEPT_FACE",FACE,{"disambiguationData":[OSD([sQuery(id+"F0.wireOp",EDGE,"E6")])]})]});
            var Q15;
            Q15=makeQuery(id+"F12.opFillet","BLEND_EDGE",EDGE,{"blendedFrom":[makeQuery(id+"F6yBhReDyAXkrBv_1.1.F4.boolean.opBoolean","COPY",EDGE,{"derivedFrom":makeQuery(id+"F6yBhReDyAXkrBv_1.1.F4.opExtrude","SWEPT_EDGE",EDGE,{"disambiguationData":[OSD([sQuery(id+"F3.wireOp",EDGE,"E23"),sQuery(id+"F3.wireOp",EDGE,"E24")])]})}),makeQuery(id+"F1.opExtrude","SWEPT_FACE",FACE,{"disambiguationData":[OSD([sQuery(id+"F0.wireOp",EDGE,"E10")])]})],"blendedInto":[makeQuery(id+"F1.opExtrude","SWEPT_FACE",FACE,{"disambiguationData":[OSD([sQuery(id+"F0.wireOp",EDGE,"E10")])]})]});
            var Q16;
            Q16=makeQuery(id+"F10.hole-0.boolean.opBoolean","INTERSECT",EDGE,{"derivedFrom":[makeQuery(id+"F8.opExtrude","CAP_FACE",FACE,{"disambiguationData":[OSD([sQuery(id+"F7.wireOp",EDGE,"E30.bottom"),sQuery(id+"F7.wireOp",EDGE,"E30.top"),sQuery(id+"F7.wireOp",EDGE,"E30.left"),sQuery(id+"F7.wireOp",EDGE,"E30.right")])],"isStart":false}),makeQuery(id+"F10.hole-0.opRevolve","SWEPT_FACE",FACE,{"disambiguationData":[OSD([sQuery(id+"F10.hole-0.sketch.wireOp",EDGE,"core_line_2")])]})]});
            var Q17;
            Q17=makeQuery(id+"F10.hole-1.boolean.opBoolean","INTERSECT",EDGE,{"derivedFrom":[makeQuery(id+"F8.opExtrude","CAP_FACE",FACE,{"disambiguationData":[OSD([sQuery(id+"F7.wireOp",EDGE,"E31.bottom"),sQuery(id+"F7.wireOp",EDGE,"E31.top"),sQuery(id+"F7.wireOp",EDGE,"E31.left"),sQuery(id+"F7.wireOp",EDGE,"E31.right")])],"isStart":false}),makeQuery(id+"F10.hole-1.opRevolve","SWEPT_FACE",FACE,{"disambiguationData":[OSD([sQuery(id+"F10.hole-1.sketch.wireOp",EDGE,"core_line_2")])]})]});
            var Q18;
            Q18=makeQuery(id+"F10.hole-2.boolean.opBoolean","INTERSECT",EDGE,{"derivedFrom":[makeQuery(id+"F8.opExtrude","CAP_FACE",FACE,{"disambiguationData":[OSD([sQuery(id+"F7.wireOp",EDGE,"E32.bottom"),sQuery(id+"F7.wireOp",EDGE,"E32.top"),sQuery(id+"F7.wireOp",EDGE,"E32.left"),sQuery(id+"F7.wireOp",EDGE,"E32.right")])],"isStart":false}),makeQuery(id+"F10.hole-2.opRevolve","SWEPT_FACE",FACE,{"disambiguationData":[OSD([sQuery(id+"F10.hole-2.sketch.wireOp",EDGE,"core_line_2")])]})]});
            var Q19;
            Q19=makeQuery(id+"F5.hole-0.boolean.opBoolean","INTERSECT",EDGE,{"derivedFrom":[makeQuery(id+"F1.opExtrude","SWEPT_FACE",FACE,{"disambiguationData":[OSD([sQuery(id+"F0.wireOp",EDGE,"E10")])]}),makeQuery(id+"F5.hole-0.opRevolve","SWEPT_FACE",FACE,{"disambiguationData":[OSD([sQuery(id+"F5.hole-0.sketch.wireOp",EDGE,"core_line_2")])]})]});
            var Q20;
            Q20=makeQuery(id+"F5.hole-1.boolean.opBoolean","INTERSECT",EDGE,{"derivedFrom":[makeQuery(id+"F1.opExtrude","SWEPT_FACE",FACE,{"disambiguationData":[OSD([sQuery(id+"F0.wireOp",EDGE,"E10")])]}),makeQuery(id+"F5.hole-1.opRevolve","SWEPT_FACE",FACE,{"disambiguationData":[OSD([sQuery(id+"F5.hole-1.sketch.wireOp",EDGE,"core_line_2")])]})]});
            var Q21;
            Q21=makeQuery(id+"F5.hole-2.boolean.opBoolean","INTERSECT",EDGE,{"derivedFrom":[makeQuery(id+"F1.opExtrude","SWEPT_FACE",FACE,{"disambiguationData":[OSD([sQuery(id+"F0.wireOp",EDGE,"E10")])]}),makeQuery(id+"F5.hole-2.opRevolve","SWEPT_FACE",FACE,{"disambiguationData":[OSD([sQuery(id+"F5.hole-2.sketch.wireOp",EDGE,"core_line_2")])]})]});
            var Q22;
            Q22=makeQuery(id+"F5.hole-2.boolean.opBoolean","INTERSECT",EDGE,{"derivedFrom":[makeQuery(id+"F1.opExtrude","SWEPT_FACE",FACE,{"disambiguationData":[OSD([sQuery(id+"F0.wireOp",EDGE,"E6")])]}),makeQuery(id+"F5.hole-2.opRevolve","SWEPT_FACE",FACE,{"disambiguationData":[OSD([sQuery(id+"F5.hole-2.sketch.wireOp",EDGE,"core_line_2")])]})]});
            var Q23;
            Q23=makeQuery(id+"F5.hole-1.boolean.opBoolean","INTERSECT",EDGE,{"derivedFrom":[makeQuery(id+"F1.opExtrude","SWEPT_FACE",FACE,{"disambiguationData":[OSD([sQuery(id+"F0.wireOp",EDGE,"E6")])]}),makeQuery(id+"F5.hole-1.opRevolve","SWEPT_FACE",FACE,{"disambiguationData":[OSD([sQuery(id+"F5.hole-1.sketch.wireOp",EDGE,"core_line_2")])]})]});
            var Q24;
            Q24=makeQuery(id+"F5.hole-0.boolean.opBoolean","INTERSECT",EDGE,{"derivedFrom":[makeQuery(id+"F1.opExtrude","SWEPT_FACE",FACE,{"disambiguationData":[OSD([sQuery(id+"F0.wireOp",EDGE,"E6")])]}),makeQuery(id+"F5.hole-0.opRevolve","SWEPT_FACE",FACE,{"disambiguationData":[OSD([sQuery(id+"F5.hole-0.sketch.wireOp",EDGE,"core_line_2")])]})]});
            chamfer(context, id + "F15", {"entities" : qUnion([Q0, Q1, Q2, Q3, Q4, Q5, Q6, Q7, Q8, Q9, Q10, Q11, Q12, Q13, Q14, Q15, Q16, Q17, Q18, Q19, Q20, Q21, Q22, Q23, Q24]), "width" : 0.76 * mm, "tangentPropagation" : true});
        }
        {
            var Q0;
            Q0=makeQuery(id+"F8.opExtrude","SWEPT_EDGE",EDGE,{"disambiguationData":[OSD([sQuery(id+"F7.wireOp",EDGE,"E30.bottom"),sQuery(id+"F7.wireOp",EDGE,"E30.left")])]});
            var Q1;
            Q1=makeQuery(id+"F8.opExtrude","SWEPT_EDGE",EDGE,{"disambiguationData":[OSD([sQuery(id+"F7.wireOp",EDGE,"E31.bottom"),sQuery(id+"F7.wireOp",EDGE,"E31.left")])]});
            var Q2;
            Q2=makeQuery(id+"F8.opExtrude","SWEPT_EDGE",EDGE,{"disambiguationData":[OSD([sQuery(id+"F7.wireOp",EDGE,"E32.bottom"),sQuery(id+"F7.wireOp",EDGE,"E32.left")])]});
            var Q3;
            Q3=makeQuery(id+"F8.opExtrude","SWEPT_EDGE",EDGE,{"disambiguationData":[OSD([sQuery(id+"F7.wireOp",EDGE,"E30.top"),sQuery(id+"F7.wireOp",EDGE,"E30.right")])]});
            var Q4;
            Q4=makeQuery(id+"F8.opExtrude","SWEPT_EDGE",EDGE,{"disambiguationData":[OSD([sQuery(id+"F7.wireOp",EDGE,"E31.top"),sQuery(id+"F7.wireOp",EDGE,"E31.right")])]});
            var Q5;
            Q5=makeQuery(id+"F8.opExtrude","SWEPT_EDGE",EDGE,{"disambiguationData":[OSD([sQuery(id+"F7.wireOp",EDGE,"E32.top"),sQuery(id+"F7.wireOp",EDGE,"E32.right")])]});
            var Q6;
            Q6=makeQuery(id+"F8.opExtrude","SWEPT_EDGE",EDGE,{"disambiguationData":[OSD([sQuery(id+"F7.wireOp",EDGE,"E30.top"),sQuery(id+"F7.wireOp",EDGE,"E30.left")])]});
            var Q7;
            Q7=makeQuery(id+"F8.opExtrude","SWEPT_EDGE",EDGE,{"disambiguationData":[OSD([sQuery(id+"F7.wireOp",EDGE,"E31.top"),sQuery(id+"F7.wireOp",EDGE,"E31.left")])]});
            var Q8;
            Q8=makeQuery(id+"F8.opExtrude","SWEPT_EDGE",EDGE,{"disambiguationData":[OSD([sQuery(id+"F7.wireOp",EDGE,"E32.top"),sQuery(id+"F7.wireOp",EDGE,"E32.left")])]});
            var Q9;
            Q9=makeQuery(id+"F8.opExtrude","SWEPT_EDGE",EDGE,{"disambiguationData":[OSD([sQuery(id+"F7.wireOp",EDGE,"E32.bottom"),sQuery(id+"F7.wireOp",EDGE,"E32.right")])]});
            var Q10;
            Q10=makeQuery(id+"F8.opExtrude","SWEPT_EDGE",EDGE,{"disambiguationData":[OSD([sQuery(id+"F7.wireOp",EDGE,"E31.bottom"),sQuery(id+"F7.wireOp",EDGE,"E31.right")])]});
            var Q11;
            Q11=makeQuery(id+"F8.opExtrude","SWEPT_EDGE",EDGE,{"disambiguationData":[OSD([sQuery(id+"F7.wireOp",EDGE,"E30.bottom"),sQuery(id+"F7.wireOp",EDGE,"E30.right")])]});
            fillet(context, id + "F16", {"entities" : qUnion([Q0, Q1, Q2, Q3, Q4, Q5, Q6, Q7, Q8, Q9, Q10, Q11]), "radius" : 1.27 * mm, "tangentPropagation" : true, "allowEdgeOverflow" : false});
        }
        {
            var Q0;
            {var subQ0=sQuery(id+"F0.wireOp",EDGE,"E0");Q0=makeQuery(id+"F2.imprint","IMPRINT",FACE,{"disambiguationData":[TD([[makeQuery(id+"F2.imprint","IMPRINT",EDGE,{"derivedFrom":makeQuery(id+"F1.opExtrude","CAP_EDGE",EDGE,{"disambiguationData":[OSD([subQ0])],"isStart":true})}),1.0]])]});}
            var sketch = newSketch(context, id + "F17", { "sketchPlane" : qUnion([Q0])});
            skLineSegment(sketch, "E36", {"start": v(-34.3, -12.7) * mm, "end": v(-35.56, -13.97) * mm});
            skLineSegment(sketch, "E37", {"start": v(-35.56, -13.97) * mm, "end": v(-35.56, -11.43) * mm});
            skLineSegment(sketch, "E38", {"start": v(-35.56, -11.43) * mm, "end": v(-34.29, -12.7) * mm});
            skSolve(sketch);
        }
        {
            var Q0;
            Q0 = qSketchRegion(id + "F17", true);
            extrude(context, id + "F18", {"entities" : qUnion([Q0]), "operationType" : NewBodyOperationType.REMOVE, "endBound" : BoundingType.THROUGH_ALL, "oppositeDirection" : true, "depth" : 25.4 * mm, "offsetDistance" : 25.4 * mm});
        }
    });
